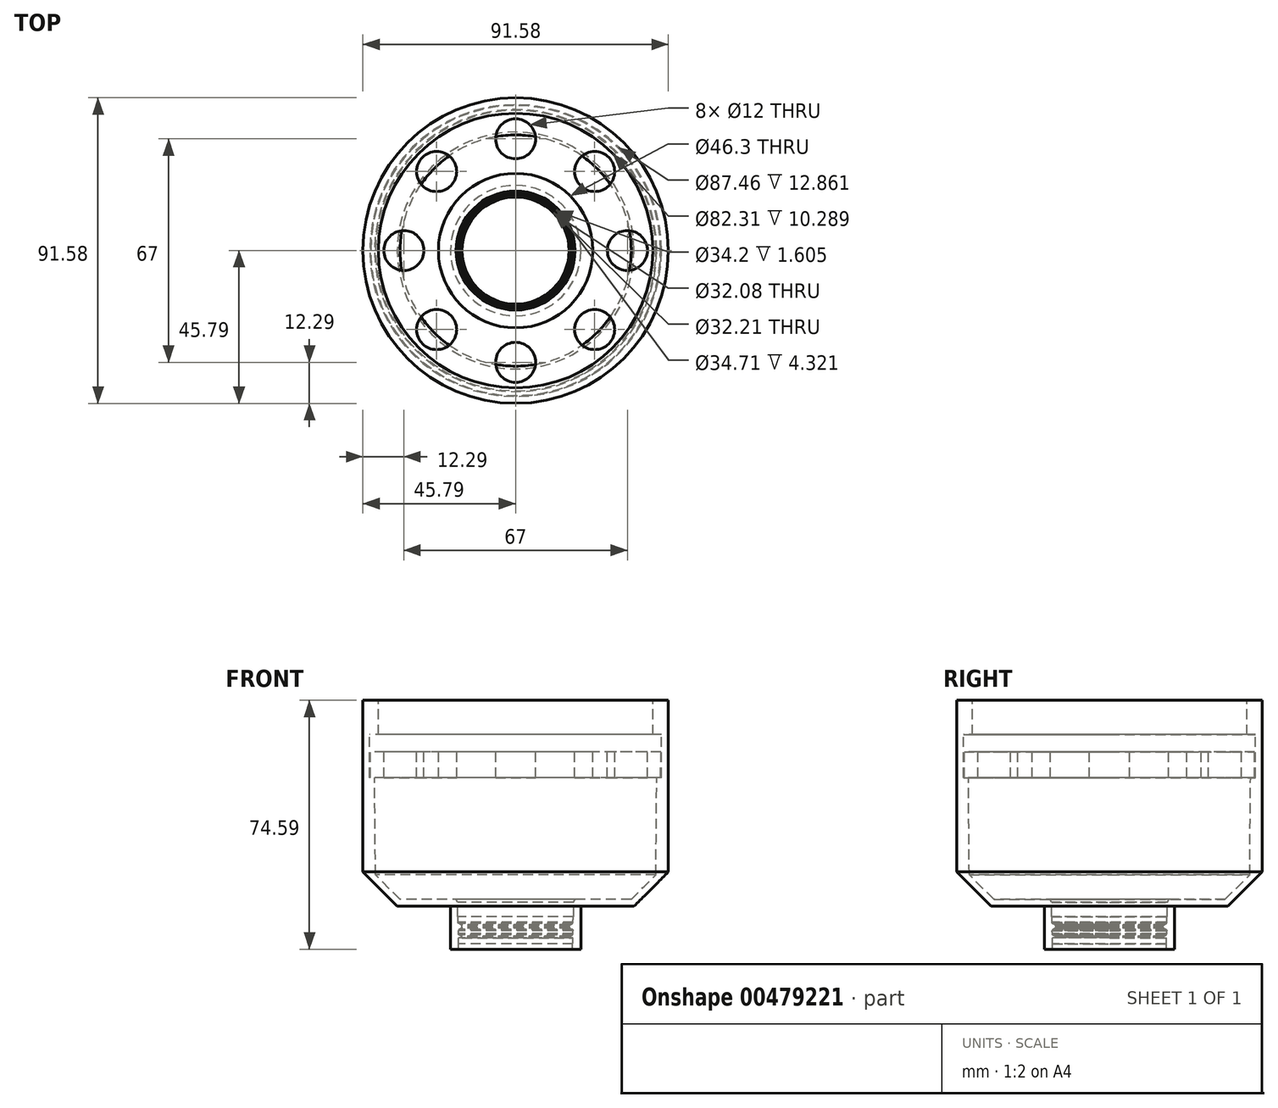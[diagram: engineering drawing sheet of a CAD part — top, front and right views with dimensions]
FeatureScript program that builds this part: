
annotation { "Feature Type Name" : "Feature", "Feature Type Description" : "" }
export const myFeature = defineFeature(function(context is Context, id is Id, definition is map)
    precondition{}
    {
        {
            var Q0;
            Q0=qCreatedBy(makeId("Front.planeOp"),FACE);
            var sketch = newSketch(context, id + "F0", { "sketchPlane" : qUnion([Q0])});
            skLineSegment(sketch, "E0", {"start": v(41.16, 37.94) * mm, "end": v(45.79, 37.94) * mm});
            skLineSegment(sketch, "E1", {"start": v(43.73, 25.08) * mm, "end": v(43.73, 27.65) * mm});
            skLineSegment(sketch, "E2", {"start": v(43.73, 27.65) * mm, "end": v(41.16, 27.65) * mm});
            skLineSegment(sketch, "E3", {"start": v(41.16, 27.65) * mm, "end": v(41.16, 37.94) * mm});
            skLineSegment(sketch, "E4", {"start": v(-41.16, 22.5) * mm, "end": v(-33.44, 22.5) * mm});
            skLineSegment(sketch, "E5", {"start": v(-43.73, 27.65) * mm, "end": v(-43.73, 25.08) * mm});
            skLineSegment(sketch, "E6", {"start": v(-41.16, 27.65) * mm, "end": v(-43.73, 27.65) * mm});
            skLineSegment(sketch, "E7", {"start": v(33.44, 22.5) * mm, "end": v(23.15, 22.5) * mm});
            skLineSegment(sketch, "E8", {"start": v(-41.16, 37.94) * mm, "end": v(-41.16, 27.65) * mm});
            skLineSegment(sketch, "E9", {"start": v(33.44, 22.5) * mm, "end": v(41.16, 22.5) * mm});
            skLineSegment(sketch, "E10", {"start": v(-23.15, 22.5) * mm, "end": v(-33.44, 22.5) * mm});
            skLineSegment(sketch, "E11", {"start": v(-43.73, 37.94) * mm, "end": v(-45.79, 37.94) * mm});
            skLineSegment(sketch, "E12", {"start": v(45.79, 37.94) * mm, "end": v(43.73, 37.94) * mm});
            skLineSegment(sketch, "E13", {"start": v(17.1, -36.65) * mm, "end": v(19.55, -36.65) * mm});
            skLineSegment(sketch, "E14", {"start": v(17.83, -21.74) * mm, "end": v(17.36, -22.56) * mm});
            skLineSegment(sketch, "E15", {"start": v(-38.42, 20.45) * mm, "end": v(-23.15, 20.45) * mm});
            skLineSegment(sketch, "E16", {"start": v(-41.42, 14.8) * mm, "end": v(-23.15, 14.8) * mm});
            skLineSegment(sketch, "E17", {"start": v(-17.83, -21.74) * mm, "end": v(-34.64, -21.74) * mm});
            skLineSegment(sketch, "E18", {"start": v(-35.5, -23.8) * mm, "end": v(-19.55, -23.8) * mm});
            skLineSegment(sketch, "E19", {"start": v(-23.15, 22.5) * mm, "end": v(-38.4, 22.5) * mm});
            skLineSegment(sketch, "E20", {"start": v(-38.4, 22.5) * mm, "end": v(-43.55, 22.5) * mm});
            skLineSegment(sketch, "E21", {"start": v(-38.42, 20.45) * mm, "end": v(-38.4, 22.5) * mm});
            skLineSegment(sketch, "E22", {"start": v(-41.37, 20.45) * mm, "end": v(-38.42, 20.45) * mm});
            skLineSegment(sketch, "E23", {"start": v(-41.42, 14.8) * mm, "end": v(-41.37, 20.45) * mm});
            skLineSegment(sketch, "E24", {"start": v(-43.48, 14.8) * mm, "end": v(-41.42, 14.8) * mm});
            skLineSegment(sketch, "E25", {"start": v(-43.55, 22.5) * mm, "end": v(-43.48, 14.8) * mm});
            skLineSegment(sketch, "E26", {"start": v(-45.79, 37.94) * mm, "end": v(-45.79, -13.5) * mm});
            skLineSegment(sketch, "E27", {"start": v(-43.73, 14.8) * mm, "end": v(-43.73, 37.94) * mm});
            skLineSegment(sketch, "E28", {"start": v(-42.29, 14.8) * mm, "end": v(-43.73, 14.8) * mm});
            skLineSegment(sketch, "E29", {"start": v(-42.03, -14.35) * mm, "end": v(-42.29, 14.8) * mm});
            skLineSegment(sketch, "E30", {"start": v(-34.64, -21.74) * mm, "end": v(-42.03, -14.35) * mm});
            skLineSegment(sketch, "E31", {"start": v(-45.79, -13.5) * mm, "end": v(-35.5, -23.8) * mm});
            skLineSegment(sketch, "E32", {"start": v(-19.57, -23.8) * mm, "end": v(-23.15, -23.8) * mm});
            skLineSegment(sketch, "E33", {"start": v(16.63, -30.81) * mm, "end": v(16.63, -30.81) * mm});
            skLineSegment(sketch, "E34", {"start": v(16.63, -30.81) * mm, "end": v(16.64, -30.81) * mm});
            skLineSegment(sketch, "E35", {"start": v(16.64, -30.81) * mm, "end": v(16.64, -30.82) * mm});
            skLineSegment(sketch, "E36", {"start": v(16.64, -30.82) * mm, "end": v(16.64, -30.82) * mm});
            skLineSegment(sketch, "E37", {"start": v(16.64, -30.82) * mm, "end": v(16.65, -30.82) * mm});
            skLineSegment(sketch, "E38", {"start": v(16.65, -30.82) * mm, "end": v(16.65, -30.82) * mm});
            skLineSegment(sketch, "E39", {"start": v(16.66, -30.84) * mm, "end": v(16.66, -30.84) * mm});
            skLineSegment(sketch, "E40", {"start": v(16.66, -30.84) * mm, "end": v(16.66, -30.83) * mm});
            skLineSegment(sketch, "E41", {"start": v(16.66, -30.83) * mm, "end": v(16.66, -30.83) * mm});
            skLineSegment(sketch, "E42", {"start": v(16.66, -30.83) * mm, "end": v(16.65, -30.83) * mm});
            skLineSegment(sketch, "E43", {"start": v(16.65, -30.83) * mm, "end": v(16.65, -30.83) * mm});
            skLineSegment(sketch, "E44", {"start": v(16.65, -30.83) * mm, "end": v(16.65, -30.82) * mm});
            skLineSegment(sketch, "E45", {"start": v(16.65, -30.82) * mm, "end": v(16.64, -30.82) * mm});
            skLineSegment(sketch, "E46", {"start": v(16.64, -30.82) * mm, "end": v(16.64, -30.81) * mm});
            skLineSegment(sketch, "E47", {"start": v(16.64, -30.81) * mm, "end": v(16.63, -30.81) * mm});
            skLineSegment(sketch, "E48", {"start": v(17.24, -26.88) * mm, "end": v(17.24, -26.88) * mm});
            skLineSegment(sketch, "E49", {"start": v(17.17, -29.4) * mm, "end": v(17.17, -29.38) * mm});
            skLineSegment(sketch, "E50", {"start": v(17.17, -29.38) * mm, "end": v(17.17, -29.37) * mm});
            skLineSegment(sketch, "E51", {"start": v(17.17, -29.37) * mm, "end": v(17.17, -29.36) * mm});
            skLineSegment(sketch, "E52", {"start": v(17.17, -29.36) * mm, "end": v(17.17, -29.35) * mm});
            skLineSegment(sketch, "E53", {"start": v(17.17, -29.35) * mm, "end": v(17.17, -29.34) * mm});
            skLineSegment(sketch, "E54", {"start": v(17.17, -29.34) * mm, "end": v(17.16, -29.32) * mm});
            skLineSegment(sketch, "E55", {"start": v(17.16, -29.32) * mm, "end": v(17.16, -29.31) * mm});
            skLineSegment(sketch, "E56", {"start": v(17.16, -29.31) * mm, "end": v(17.16, -29.3) * mm});
            skLineSegment(sketch, "E57", {"start": v(17.16, -29.3) * mm, "end": v(17.16, -29.29) * mm});
            skLineSegment(sketch, "E58", {"start": v(17.16, -29.29) * mm, "end": v(17.16, -29.28) * mm});
            skLineSegment(sketch, "E59", {"start": v(17.16, -29.28) * mm, "end": v(17.15, -29.27) * mm});
            skLineSegment(sketch, "E60", {"start": v(17.15, -29.27) * mm, "end": v(17.15, -29.26) * mm});
            skLineSegment(sketch, "E61", {"start": v(17.15, -29.26) * mm, "end": v(17.14, -29.24) * mm});
            skLineSegment(sketch, "E62", {"start": v(17.14, -29.24) * mm, "end": v(17.14, -29.23) * mm});
            skLineSegment(sketch, "E63", {"start": v(17.14, -29.23) * mm, "end": v(17.14, -29.22) * mm});
            skLineSegment(sketch, "E64", {"start": v(17.14, -29.22) * mm, "end": v(17.13, -29.21) * mm});
            skLineSegment(sketch, "E65", {"start": v(17.13, -29.21) * mm, "end": v(17.13, -29.2) * mm});
            skLineSegment(sketch, "E66", {"start": v(17.13, -29.2) * mm, "end": v(17.12, -29.2) * mm});
            skLineSegment(sketch, "E67", {"start": v(17.12, -29.2) * mm, "end": v(17.12, -29.18) * mm});
            skLineSegment(sketch, "E68", {"start": v(17.12, -29.18) * mm, "end": v(17.11, -29.18) * mm});
            skLineSegment(sketch, "E69", {"start": v(17.11, -29.18) * mm, "end": v(17.1, -29.17) * mm});
            skLineSegment(sketch, "E70", {"start": v(17.1, -29.17) * mm, "end": v(17.1, -29.16) * mm});
            skLineSegment(sketch, "E71", {"start": v(17.1, -29.16) * mm, "end": v(17.1, -29.15) * mm});
            skLineSegment(sketch, "E72", {"start": v(17.1, -29.15) * mm, "end": v(17.09, -29.14) * mm});
            skLineSegment(sketch, "E73", {"start": v(16.23, -27.73) * mm, "end": v(16.24, -27.73) * mm});
            skLineSegment(sketch, "E74", {"start": v(16.24, -27.73) * mm, "end": v(16.24, -27.72) * mm});
            skLineSegment(sketch, "E75", {"start": v(16.24, -27.72) * mm, "end": v(16.25, -27.72) * mm});
            skLineSegment(sketch, "E76", {"start": v(16.25, -27.72) * mm, "end": v(16.25, -27.71) * mm});
            skLineSegment(sketch, "E77", {"start": v(16.25, -27.71) * mm, "end": v(16.25, -27.71) * mm});
            skLineSegment(sketch, "E78", {"start": v(16.25, -27.71) * mm, "end": v(16.26, -27.7) * mm});
            skLineSegment(sketch, "E79", {"start": v(16.26, -27.7) * mm, "end": v(16.26, -27.7) * mm});
            skLineSegment(sketch, "E80", {"start": v(16.26, -27.7) * mm, "end": v(16.27, -27.7) * mm});
            skLineSegment(sketch, "E81", {"start": v(16.27, -27.7) * mm, "end": v(16.27, -27.7) * mm});
            skLineSegment(sketch, "E82", {"start": v(16.27, -27.7) * mm, "end": v(16.27, -27.69) * mm});
            skLineSegment(sketch, "E83", {"start": v(16.27, -27.69) * mm, "end": v(16.28, -27.69) * mm});
            skLineSegment(sketch, "E84", {"start": v(16.28, -27.69) * mm, "end": v(16.28, -27.68) * mm});
            skLineSegment(sketch, "E85", {"start": v(16.28, -27.68) * mm, "end": v(16.29, -27.68) * mm});
            skLineSegment(sketch, "E86", {"start": v(16.29, -27.68) * mm, "end": v(16.3, -27.67) * mm});
            skLineSegment(sketch, "E87", {"start": v(16.3, -27.67) * mm, "end": v(16.3, -27.67) * mm});
            skLineSegment(sketch, "E88", {"start": v(16.3, -27.67) * mm, "end": v(16.3, -27.66) * mm});
            skLineSegment(sketch, "E89", {"start": v(16.3, -27.66) * mm, "end": v(16.31, -27.66) * mm});
            skLineSegment(sketch, "E90", {"start": v(16.31, -27.66) * mm, "end": v(16.32, -27.66) * mm});
            skLineSegment(sketch, "E91", {"start": v(16.32, -27.66) * mm, "end": v(16.32, -27.65) * mm});
            skLineSegment(sketch, "E92", {"start": v(16.32, -27.65) * mm, "end": v(16.32, -27.65) * mm});
            skLineSegment(sketch, "E93", {"start": v(16.32, -27.65) * mm, "end": v(16.33, -27.65) * mm});
            skLineSegment(sketch, "E94", {"start": v(16.33, -27.65) * mm, "end": v(16.33, -27.65) * mm});
            skLineSegment(sketch, "E95", {"start": v(16.33, -27.65) * mm, "end": v(16.34, -27.64) * mm});
            skLineSegment(sketch, "E96", {"start": v(16.34, -27.64) * mm, "end": v(16.37, -27.62) * mm});
            skLineSegment(sketch, "E97", {"start": v(16.37, -27.62) * mm, "end": v(16.4, -27.6) * mm});
            skLineSegment(sketch, "E98", {"start": v(16.4, -27.6) * mm, "end": v(16.42, -27.59) * mm});
            skLineSegment(sketch, "E99", {"start": v(16.42, -27.59) * mm, "end": v(16.45, -27.57) * mm});
            skLineSegment(sketch, "E100", {"start": v(16.45, -27.57) * mm, "end": v(16.48, -27.55) * mm});
            skLineSegment(sketch, "E101", {"start": v(16.48, -27.55) * mm, "end": v(16.5, -27.54) * mm});
            skLineSegment(sketch, "E102", {"start": v(16.5, -27.54) * mm, "end": v(16.54, -27.52) * mm});
            skLineSegment(sketch, "E103", {"start": v(16.54, -27.52) * mm, "end": v(16.57, -27.5) * mm});
            skLineSegment(sketch, "E104", {"start": v(16.57, -27.5) * mm, "end": v(16.6, -27.48) * mm});
            skLineSegment(sketch, "E105", {"start": v(16.6, -27.48) * mm, "end": v(16.62, -27.47) * mm});
            skLineSegment(sketch, "E106", {"start": v(16.62, -27.47) * mm, "end": v(16.65, -27.45) * mm});
            skLineSegment(sketch, "E107", {"start": v(16.65, -27.45) * mm, "end": v(16.68, -27.43) * mm});
            skLineSegment(sketch, "E108", {"start": v(16.68, -27.43) * mm, "end": v(16.7, -27.41) * mm});
            skLineSegment(sketch, "E109", {"start": v(16.7, -27.41) * mm, "end": v(16.74, -27.4) * mm});
            skLineSegment(sketch, "E110", {"start": v(16.74, -27.4) * mm, "end": v(16.76, -27.38) * mm});
            skLineSegment(sketch, "E111", {"start": v(16.76, -27.38) * mm, "end": v(16.8, -27.36) * mm});
            skLineSegment(sketch, "E112", {"start": v(16.8, -27.36) * mm, "end": v(16.82, -27.34) * mm});
            skLineSegment(sketch, "E113", {"start": v(16.82, -27.34) * mm, "end": v(16.85, -27.32) * mm});
            skLineSegment(sketch, "E114", {"start": v(16.85, -27.32) * mm, "end": v(16.88, -27.3) * mm});
            skLineSegment(sketch, "E115", {"start": v(16.88, -27.3) * mm, "end": v(16.9, -27.29) * mm});
            skLineSegment(sketch, "E116", {"start": v(16.9, -27.29) * mm, "end": v(16.93, -27.27) * mm});
            skLineSegment(sketch, "E117", {"start": v(16.93, -27.27) * mm, "end": v(16.96, -27.25) * mm});
            skLineSegment(sketch, "E118", {"start": v(16.96, -27.25) * mm, "end": v(17, -27.23) * mm});
            skLineSegment(sketch, "E119", {"start": v(17, -27.23) * mm, "end": v(17.02, -27.22) * mm});
            skLineSegment(sketch, "E120", {"start": v(17.02, -27.22) * mm, "end": v(17.02, -27.21) * mm});
            skLineSegment(sketch, "E121", {"start": v(17.02, -27.21) * mm, "end": v(17.02, -27.21) * mm});
            skLineSegment(sketch, "E122", {"start": v(17.02, -27.21) * mm, "end": v(17.03, -27.21) * mm});
            skLineSegment(sketch, "E123", {"start": v(17.03, -27.21) * mm, "end": v(17.03, -27.2) * mm});
            skLineSegment(sketch, "E124", {"start": v(17.03, -27.2) * mm, "end": v(17.03, -27.2) * mm});
            skLineSegment(sketch, "E125", {"start": v(17.03, -27.2) * mm, "end": v(17.04, -27.2) * mm});
            skLineSegment(sketch, "E126", {"start": v(17.04, -27.2) * mm, "end": v(17.04, -27.2) * mm});
            skLineSegment(sketch, "E127", {"start": v(17.04, -27.2) * mm, "end": v(17.05, -27.2) * mm});
            skLineSegment(sketch, "E128", {"start": v(17.05, -27.2) * mm, "end": v(17.05, -27.2) * mm});
            skLineSegment(sketch, "E129", {"start": v(17.05, -27.2) * mm, "end": v(17.06, -27.19) * mm});
            skLineSegment(sketch, "E130", {"start": v(17.06, -27.19) * mm, "end": v(17.06, -27.19) * mm});
            skLineSegment(sketch, "E131", {"start": v(17.06, -27.19) * mm, "end": v(17.06, -27.18) * mm});
            skLineSegment(sketch, "E132", {"start": v(17.06, -27.18) * mm, "end": v(17.06, -27.18) * mm});
            skLineSegment(sketch, "E133", {"start": v(17.06, -27.18) * mm, "end": v(17.07, -27.18) * mm});
            skLineSegment(sketch, "E134", {"start": v(17.07, -27.18) * mm, "end": v(17.07, -27.18) * mm});
            skLineSegment(sketch, "E135", {"start": v(17.07, -27.18) * mm, "end": v(17.07, -27.17) * mm});
            skLineSegment(sketch, "E136", {"start": v(17.07, -27.17) * mm, "end": v(17.07, -27.17) * mm});
            skLineSegment(sketch, "E137", {"start": v(17.07, -27.17) * mm, "end": v(17.08, -27.17) * mm});
            skLineSegment(sketch, "E138", {"start": v(17.08, -27.17) * mm, "end": v(17.09, -27.16) * mm});
            skLineSegment(sketch, "E139", {"start": v(17.09, -27.16) * mm, "end": v(17.1, -27.15) * mm});
            skLineSegment(sketch, "E140", {"start": v(17.1, -27.15) * mm, "end": v(17.1, -27.14) * mm});
            skLineSegment(sketch, "E141", {"start": v(17.1, -27.14) * mm, "end": v(17.11, -27.13) * mm});
            skLineSegment(sketch, "E142", {"start": v(17.11, -27.13) * mm, "end": v(17.12, -27.12) * mm});
            skLineSegment(sketch, "E143", {"start": v(17.12, -27.12) * mm, "end": v(17.13, -27.11) * mm});
            skLineSegment(sketch, "E144", {"start": v(17.13, -27.11) * mm, "end": v(17.13, -27.1) * mm});
            skLineSegment(sketch, "E145", {"start": v(17.13, -27.1) * mm, "end": v(17.14, -27.1) * mm});
            skLineSegment(sketch, "E146", {"start": v(17.14, -27.1) * mm, "end": v(17.15, -27.08) * mm});
            skLineSegment(sketch, "E147", {"start": v(17.15, -27.08) * mm, "end": v(17.16, -27.07) * mm});
            skLineSegment(sketch, "E148", {"start": v(17.16, -27.07) * mm, "end": v(17.16, -27.06) * mm});
            skLineSegment(sketch, "E149", {"start": v(17.16, -27.06) * mm, "end": v(17.17, -27.05) * mm});
            skLineSegment(sketch, "E150", {"start": v(17.17, -27.05) * mm, "end": v(17.17, -27.03) * mm});
            skLineSegment(sketch, "E151", {"start": v(17.17, -27.03) * mm, "end": v(17.18, -27.02) * mm});
            skLineSegment(sketch, "E152", {"start": v(17.18, -27.02) * mm, "end": v(17.19, -27) * mm});
            skLineSegment(sketch, "E153", {"start": v(17.19, -27) * mm, "end": v(17.2, -27) * mm});
            skLineSegment(sketch, "E154", {"start": v(17.2, -27) * mm, "end": v(17.2, -26.98) * mm});
            skLineSegment(sketch, "E155", {"start": v(17.2, -26.98) * mm, "end": v(17.2, -26.97) * mm});
            skLineSegment(sketch, "E156", {"start": v(17.2, -26.97) * mm, "end": v(17.2, -26.95) * mm});
            skLineSegment(sketch, "E157", {"start": v(17.2, -26.95) * mm, "end": v(17.2, -26.94) * mm});
            skLineSegment(sketch, "E158", {"start": v(17.2, -26.94) * mm, "end": v(17.2, -26.92) * mm});
            skLineSegment(sketch, "E159", {"start": v(17.2, -26.92) * mm, "end": v(17.21, -26.9) * mm});
            skLineSegment(sketch, "E160", {"start": v(17.21, -26.9) * mm, "end": v(17.21, -26.9) * mm});
            skLineSegment(sketch, "E161", {"start": v(17.21, -26.9) * mm, "end": v(17.21, -26.88) * mm});
            skLineSegment(sketch, "E162", {"start": v(17.2, -29.43) * mm, "end": v(17.2, -29.43) * mm});
            skLineSegment(sketch, "E163", {"start": v(17.2, -29.43) * mm, "end": v(17.2, -29.42) * mm});
            skLineSegment(sketch, "E164", {"start": v(17.2, -29.42) * mm, "end": v(17.2, -29.42) * mm});
            skLineSegment(sketch, "E165", {"start": v(17.2, -29.42) * mm, "end": v(17.2, -29.41) * mm});
            skLineSegment(sketch, "E166", {"start": v(17.2, -29.41) * mm, "end": v(17.2, -29.41) * mm});
            skLineSegment(sketch, "E167", {"start": v(17.2, -29.41) * mm, "end": v(17.19, -29.4) * mm});
            skLineSegment(sketch, "E168", {"start": v(17.19, -29.4) * mm, "end": v(17.19, -29.4) * mm});
            skLineSegment(sketch, "E169", {"start": v(17.19, -29.4) * mm, "end": v(17.18, -29.4) * mm});
            skLineSegment(sketch, "E170", {"start": v(17.18, -29.4) * mm, "end": v(17.18, -29.4) * mm});
            skLineSegment(sketch, "E171", {"start": v(17.18, -29.4) * mm, "end": v(17.17, -29.4) * mm});
            skLineSegment(sketch, "E172", {"start": v(17.17, -29.4) * mm, "end": v(17.17, -29.4) * mm});
            skLineSegment(sketch, "E173", {"start": v(17.02, -27.22) * mm, "end": v(17.02, -27.22) * mm});
            skLineSegment(sketch, "E174", {"start": v(17.02, -27.22) * mm, "end": v(17.03, -27.22) * mm});
            skLineSegment(sketch, "E175", {"start": v(17.03, -27.22) * mm, "end": v(17.03, -27.22) * mm});
            skLineSegment(sketch, "E176", {"start": v(17.03, -27.22) * mm, "end": v(17.03, -27.23) * mm});
            skLineSegment(sketch, "E177", {"start": v(17.03, -27.23) * mm, "end": v(17.03, -27.23) * mm});
            skLineSegment(sketch, "E178", {"start": v(17.03, -27.23) * mm, "end": v(17.04, -27.23) * mm});
            skLineSegment(sketch, "E179", {"start": v(17.04, -27.23) * mm, "end": v(17.04, -27.23) * mm});
            skLineSegment(sketch, "E180", {"start": v(17.04, -27.23) * mm, "end": v(17.04, -27.24) * mm});
            skLineSegment(sketch, "E181", {"start": v(17.04, -27.24) * mm, "end": v(17.04, -27.24) * mm});
            skLineSegment(sketch, "E182", {"start": v(17.24, -26.88) * mm, "end": v(17.23, -26.88) * mm});
            skLineSegment(sketch, "E183", {"start": v(17.23, -26.88) * mm, "end": v(17.23, -26.88) * mm});
            skLineSegment(sketch, "E184", {"start": v(17.23, -26.88) * mm, "end": v(17.22, -26.88) * mm});
            skLineSegment(sketch, "E185", {"start": v(17.22, -26.88) * mm, "end": v(17.22, -26.88) * mm});
            skLineSegment(sketch, "E186", {"start": v(17.22, -26.88) * mm, "end": v(17.21, -26.88) * mm});
            skLineSegment(sketch, "E187", {"start": v(17.21, -26.88) * mm, "end": v(17.21, -26.88) * mm});
            skLineSegment(sketch, "E188", {"start": v(17.24, -26.88) * mm, "end": v(17.24, -26.89) * mm});
            skLineSegment(sketch, "E189", {"start": v(17.24, -26.89) * mm, "end": v(17.24, -26.89) * mm});
            skLineSegment(sketch, "E190", {"start": v(17.24, -26.89) * mm, "end": v(17.24, -26.9) * mm});
            skLineSegment(sketch, "E191", {"start": v(17.24, -26.9) * mm, "end": v(17.24, -26.9) * mm});
            skLineSegment(sketch, "E192", {"start": v(-17.36, -22.56) * mm, "end": v(-17.83, -21.74) * mm});
            skLineSegment(sketch, "E193", {"start": v(-17.36, -26.88) * mm, "end": v(-17.36, -22.56) * mm});
            skLineSegment(sketch, "E194", {"start": v(-17.24, -26.88) * mm, "end": v(-17.36, -26.88) * mm});
            skLineSegment(sketch, "E195", {"start": v(-17.21, -28.6) * mm, "end": v(-17.24, -26.88) * mm});
            skLineSegment(sketch, "E196", {"start": v(-17, -28.96) * mm, "end": v(-17.02, -28.95) * mm});
            skLineSegment(sketch, "E197", {"start": v(-17.02, -28.95) * mm, "end": v(-17.04, -28.94) * mm});
            skLineSegment(sketch, "E198", {"start": v(-17.04, -28.94) * mm, "end": v(-17.05, -28.93) * mm});
            skLineSegment(sketch, "E199", {"start": v(-17.05, -28.93) * mm, "end": v(-17.07, -28.92) * mm});
            skLineSegment(sketch, "E200", {"start": v(-17.07, -28.92) * mm, "end": v(-17.08, -28.9) * mm});
            skLineSegment(sketch, "E201", {"start": v(-17.08, -28.9) * mm, "end": v(-17.1, -28.9) * mm});
            skLineSegment(sketch, "E202", {"start": v(-17.1, -28.9) * mm, "end": v(-17.1, -28.88) * mm});
            skLineSegment(sketch, "E203", {"start": v(-17.1, -28.88) * mm, "end": v(-17.12, -28.87) * mm});
            skLineSegment(sketch, "E204", {"start": v(-17.12, -28.87) * mm, "end": v(-17.13, -28.85) * mm});
            skLineSegment(sketch, "E205", {"start": v(-17.13, -28.85) * mm, "end": v(-17.14, -28.84) * mm});
            skLineSegment(sketch, "E206", {"start": v(-17.14, -28.84) * mm, "end": v(-17.15, -28.82) * mm});
            skLineSegment(sketch, "E207", {"start": v(-17.15, -28.82) * mm, "end": v(-17.16, -28.8) * mm});
            skLineSegment(sketch, "E208", {"start": v(-17.16, -28.8) * mm, "end": v(-17.17, -28.8) * mm});
            skLineSegment(sketch, "E209", {"start": v(-17.17, -28.8) * mm, "end": v(-17.17, -28.78) * mm});
            skLineSegment(sketch, "E210", {"start": v(-17.17, -28.78) * mm, "end": v(-17.18, -28.76) * mm});
            skLineSegment(sketch, "E211", {"start": v(-17.18, -28.76) * mm, "end": v(-17.19, -28.75) * mm});
            skLineSegment(sketch, "E212", {"start": v(-17.19, -28.75) * mm, "end": v(-17.2, -28.73) * mm});
            skLineSegment(sketch, "E213", {"start": v(-17.2, -28.73) * mm, "end": v(-17.2, -28.71) * mm});
            skLineSegment(sketch, "E214", {"start": v(-17.2, -28.71) * mm, "end": v(-17.2, -28.7) * mm});
            skLineSegment(sketch, "E215", {"start": v(-17.2, -28.7) * mm, "end": v(-17.2, -28.68) * mm});
            skLineSegment(sketch, "E216", {"start": v(-17.2, -28.68) * mm, "end": v(-17.2, -28.66) * mm});
            skLineSegment(sketch, "E217", {"start": v(-17.2, -28.66) * mm, "end": v(-17.21, -28.64) * mm});
            skLineSegment(sketch, "E218", {"start": v(-17.21, -28.64) * mm, "end": v(-17.21, -28.62) * mm});
            skLineSegment(sketch, "E219", {"start": v(-17.21, -28.62) * mm, "end": v(-17.21, -28.6) * mm});
            skLineSegment(sketch, "E220", {"start": v(-16.3, -29.36) * mm, "end": v(-16.34, -29.34) * mm});
            skLineSegment(sketch, "E221", {"start": v(-16.34, -29.34) * mm, "end": v(-16.37, -29.33) * mm});
            skLineSegment(sketch, "E222", {"start": v(-16.37, -29.33) * mm, "end": v(-16.4, -29.31) * mm});
            skLineSegment(sketch, "E223", {"start": v(-16.4, -29.31) * mm, "end": v(-16.43, -29.3) * mm});
            skLineSegment(sketch, "E224", {"start": v(-16.43, -29.3) * mm, "end": v(-16.45, -29.28) * mm});
            skLineSegment(sketch, "E225", {"start": v(-16.45, -29.28) * mm, "end": v(-16.48, -29.26) * mm});
            skLineSegment(sketch, "E226", {"start": v(-16.48, -29.26) * mm, "end": v(-16.51, -29.24) * mm});
            skLineSegment(sketch, "E227", {"start": v(-16.51, -29.24) * mm, "end": v(-16.54, -29.23) * mm});
            skLineSegment(sketch, "E228", {"start": v(-16.54, -29.23) * mm, "end": v(-16.57, -29.2) * mm});
            skLineSegment(sketch, "E229", {"start": v(-16.57, -29.2) * mm, "end": v(-16.6, -29.2) * mm});
            skLineSegment(sketch, "E230", {"start": v(-16.6, -29.2) * mm, "end": v(-16.63, -29.18) * mm});
            skLineSegment(sketch, "E231", {"start": v(-16.63, -29.18) * mm, "end": v(-16.66, -29.16) * mm});
            skLineSegment(sketch, "E232", {"start": v(-16.66, -29.16) * mm, "end": v(-16.69, -29.14) * mm});
            skLineSegment(sketch, "E233", {"start": v(-16.69, -29.14) * mm, "end": v(-16.72, -29.12) * mm});
            skLineSegment(sketch, "E234", {"start": v(-16.72, -29.12) * mm, "end": v(-16.75, -29.1) * mm});
            skLineSegment(sketch, "E235", {"start": v(-16.75, -29.1) * mm, "end": v(-16.77, -29.1) * mm});
            skLineSegment(sketch, "E236", {"start": v(-16.77, -29.1) * mm, "end": v(-16.8, -29.07) * mm});
            skLineSegment(sketch, "E237", {"start": v(-16.8, -29.07) * mm, "end": v(-16.83, -29.06) * mm});
            skLineSegment(sketch, "E238", {"start": v(-16.83, -29.06) * mm, "end": v(-16.86, -29.04) * mm});
            skLineSegment(sketch, "E239", {"start": v(-16.86, -29.04) * mm, "end": v(-16.9, -29.02) * mm});
            skLineSegment(sketch, "E240", {"start": v(-16.9, -29.02) * mm, "end": v(-16.92, -29) * mm});
            skLineSegment(sketch, "E241", {"start": v(-16.92, -29) * mm, "end": v(-16.95, -29) * mm});
            skLineSegment(sketch, "E242", {"start": v(-16.95, -29) * mm, "end": v(-16.98, -28.97) * mm});
            skLineSegment(sketch, "E243", {"start": v(-16.98, -28.97) * mm, "end": v(-17, -28.96) * mm});
            skLineSegment(sketch, "E244", {"start": v(-16.1, -29.72) * mm, "end": v(-16.1, -29.7) * mm});
            skLineSegment(sketch, "E245", {"start": v(-16.1, -29.7) * mm, "end": v(-16.1, -29.68) * mm});
            skLineSegment(sketch, "E246", {"start": v(-16.1, -29.68) * mm, "end": v(-16.1, -29.66) * mm});
            skLineSegment(sketch, "E247", {"start": v(-16.1, -29.66) * mm, "end": v(-16.1, -29.65) * mm});
            skLineSegment(sketch, "E248", {"start": v(-16.1, -29.65) * mm, "end": v(-16.11, -29.63) * mm});
            skLineSegment(sketch, "E249", {"start": v(-16.11, -29.63) * mm, "end": v(-16.12, -29.61) * mm});
            skLineSegment(sketch, "E250", {"start": v(-16.12, -29.61) * mm, "end": v(-16.12, -29.6) * mm});
            skLineSegment(sketch, "E251", {"start": v(-16.12, -29.6) * mm, "end": v(-16.13, -29.58) * mm});
            skLineSegment(sketch, "E252", {"start": v(-16.13, -29.58) * mm, "end": v(-16.13, -29.56) * mm});
            skLineSegment(sketch, "E253", {"start": v(-16.13, -29.56) * mm, "end": v(-16.14, -29.54) * mm});
            skLineSegment(sketch, "E254", {"start": v(-16.14, -29.54) * mm, "end": v(-16.15, -29.53) * mm});
            skLineSegment(sketch, "E255", {"start": v(-16.15, -29.53) * mm, "end": v(-16.16, -29.51) * mm});
            skLineSegment(sketch, "E256", {"start": v(-16.16, -29.51) * mm, "end": v(-16.17, -29.5) * mm});
            skLineSegment(sketch, "E257", {"start": v(-16.17, -29.5) * mm, "end": v(-16.18, -29.48) * mm});
            skLineSegment(sketch, "E258", {"start": v(-16.18, -29.48) * mm, "end": v(-16.19, -29.47) * mm});
            skLineSegment(sketch, "E259", {"start": v(-16.19, -29.47) * mm, "end": v(-16.2, -29.45) * mm});
            skLineSegment(sketch, "E260", {"start": v(-16.2, -29.45) * mm, "end": v(-16.21, -29.44) * mm});
            skLineSegment(sketch, "E261", {"start": v(-16.21, -29.44) * mm, "end": v(-16.22, -29.43) * mm});
            skLineSegment(sketch, "E262", {"start": v(-16.22, -29.43) * mm, "end": v(-16.24, -29.41) * mm});
            skLineSegment(sketch, "E263", {"start": v(-16.24, -29.41) * mm, "end": v(-16.25, -29.4) * mm});
            skLineSegment(sketch, "E264", {"start": v(-16.25, -29.4) * mm, "end": v(-16.26, -29.4) * mm});
            skLineSegment(sketch, "E265", {"start": v(-16.26, -29.4) * mm, "end": v(-16.28, -29.38) * mm});
            skLineSegment(sketch, "E266", {"start": v(-16.28, -29.38) * mm, "end": v(-16.3, -29.37) * mm});
            skLineSegment(sketch, "E267", {"start": v(-16.3, -29.37) * mm, "end": v(-16.3, -29.36) * mm});
            skLineSegment(sketch, "E268", {"start": v(-16.1, -29.88) * mm, "end": v(-16.1, -29.87) * mm});
            skLineSegment(sketch, "E269", {"start": v(-16.1, -29.87) * mm, "end": v(-16.1, -29.87) * mm});
            skLineSegment(sketch, "E270", {"start": v(-16.1, -29.87) * mm, "end": v(-16.1, -29.86) * mm});
            skLineSegment(sketch, "E271", {"start": v(-16.1, -29.86) * mm, "end": v(-16.1, -29.85) * mm});
            skLineSegment(sketch, "E272", {"start": v(-16.1, -29.85) * mm, "end": v(-16.1, -29.85) * mm});
            skLineSegment(sketch, "E273", {"start": v(-16.1, -29.85) * mm, "end": v(-16.1, -29.84) * mm});
            skLineSegment(sketch, "E274", {"start": v(-16.1, -29.84) * mm, "end": v(-16.1, -29.83) * mm});
            skLineSegment(sketch, "E275", {"start": v(-16.1, -29.83) * mm, "end": v(-16.1, -29.83) * mm});
            skLineSegment(sketch, "E276", {"start": v(-16.1, -29.83) * mm, "end": v(-16.1, -29.82) * mm});
            skLineSegment(sketch, "E277", {"start": v(-16.1, -29.82) * mm, "end": v(-16.1, -29.81) * mm});
            skLineSegment(sketch, "E278", {"start": v(-16.1, -29.81) * mm, "end": v(-16.1, -29.8) * mm});
            skLineSegment(sketch, "E279", {"start": v(-16.1, -29.8) * mm, "end": v(-16.1, -29.8) * mm});
            skLineSegment(sketch, "E280", {"start": v(-16.1, -29.8) * mm, "end": v(-16.1, -29.79) * mm});
            skLineSegment(sketch, "E281", {"start": v(-16.1, -29.79) * mm, "end": v(-16.1, -29.78) * mm});
            skLineSegment(sketch, "E282", {"start": v(-16.1, -29.78) * mm, "end": v(-16.1, -29.77) * mm});
            skLineSegment(sketch, "E283", {"start": v(-16.1, -29.77) * mm, "end": v(-16.1, -29.76) * mm});
            skLineSegment(sketch, "E284", {"start": v(-16.1, -29.76) * mm, "end": v(-16.1, -29.76) * mm});
            skLineSegment(sketch, "E285", {"start": v(-16.1, -29.76) * mm, "end": v(-16.1, -29.75) * mm});
            skLineSegment(sketch, "E286", {"start": v(-16.1, -29.75) * mm, "end": v(-16.1, -29.74) * mm});
            skLineSegment(sketch, "E287", {"start": v(-16.1, -29.74) * mm, "end": v(-16.1, -29.74) * mm});
            skLineSegment(sketch, "E288", {"start": v(-16.1, -29.74) * mm, "end": v(-16.1, -29.73) * mm});
            skLineSegment(sketch, "E289", {"start": v(-16.1, -29.73) * mm, "end": v(-16.1, -29.72) * mm});
            skLineSegment(sketch, "E290", {"start": v(-16.1, -29.72) * mm, "end": v(-16.1, -29.72) * mm});
            skLineSegment(sketch, "E291", {"start": v(-16.1, -30.04) * mm, "end": v(-16.1, -30.04) * mm});
            skLineSegment(sketch, "E292", {"start": v(-16.1, -30.04) * mm, "end": v(-16.1, -30.03) * mm});
            skLineSegment(sketch, "E293", {"start": v(-16.1, -30.03) * mm, "end": v(-16.1, -30.02) * mm});
            skLineSegment(sketch, "E294", {"start": v(-16.1, -30.02) * mm, "end": v(-16.1, -30.02) * mm});
            skLineSegment(sketch, "E295", {"start": v(-16.1, -30.02) * mm, "end": v(-16.1, -30.01) * mm});
            skLineSegment(sketch, "E296", {"start": v(-16.1, -30.01) * mm, "end": v(-16.1, -30) * mm});
            skLineSegment(sketch, "E297", {"start": v(-16.1, -30) * mm, "end": v(-16.1, -30) * mm});
            skLineSegment(sketch, "E298", {"start": v(-16.1, -30) * mm, "end": v(-16.1, -29.99) * mm});
            skLineSegment(sketch, "E299", {"start": v(-16.1, -29.99) * mm, "end": v(-16.1, -29.98) * mm});
            skLineSegment(sketch, "E300", {"start": v(-16.1, -29.98) * mm, "end": v(-16.1, -29.98) * mm});
            skLineSegment(sketch, "E301", {"start": v(-16.1, -29.98) * mm, "end": v(-16.1, -29.97) * mm});
            skLineSegment(sketch, "E302", {"start": v(-16.1, -29.97) * mm, "end": v(-16.1, -29.96) * mm});
            skLineSegment(sketch, "E303", {"start": v(-16.1, -29.96) * mm, "end": v(-16.1, -29.96) * mm});
            skLineSegment(sketch, "E304", {"start": v(-16.1, -29.96) * mm, "end": v(-16.1, -29.95) * mm});
            skLineSegment(sketch, "E305", {"start": v(-16.1, -29.95) * mm, "end": v(-16.1, -29.94) * mm});
            skLineSegment(sketch, "E306", {"start": v(-16.1, -29.94) * mm, "end": v(-16.1, -29.94) * mm});
            skLineSegment(sketch, "E307", {"start": v(-16.1, -29.94) * mm, "end": v(-16.1, -29.93) * mm});
            skLineSegment(sketch, "E308", {"start": v(-16.1, -29.93) * mm, "end": v(-16.1, -29.92) * mm});
            skLineSegment(sketch, "E309", {"start": v(-16.1, -29.92) * mm, "end": v(-16.1, -29.91) * mm});
            skLineSegment(sketch, "E310", {"start": v(-16.1, -29.91) * mm, "end": v(-16.1, -29.9) * mm});
            skLineSegment(sketch, "E311", {"start": v(-16.1, -29.9) * mm, "end": v(-16.1, -29.9) * mm});
            skLineSegment(sketch, "E312", {"start": v(-16.1, -29.9) * mm, "end": v(-16.1, -29.89) * mm});
            skLineSegment(sketch, "E313", {"start": v(-16.1, -29.89) * mm, "end": v(-16.1, -29.88) * mm});
            skLineSegment(sketch, "E314", {"start": v(-16.3, -30.4) * mm, "end": v(-16.3, -30.4) * mm});
            skLineSegment(sketch, "E315", {"start": v(-16.3, -30.4) * mm, "end": v(-16.28, -30.38) * mm});
            skLineSegment(sketch, "E316", {"start": v(-16.28, -30.38) * mm, "end": v(-16.26, -30.37) * mm});
            skLineSegment(sketch, "E317", {"start": v(-16.26, -30.37) * mm, "end": v(-16.25, -30.36) * mm});
            skLineSegment(sketch, "E318", {"start": v(-16.25, -30.36) * mm, "end": v(-16.24, -30.35) * mm});
            skLineSegment(sketch, "E319", {"start": v(-16.24, -30.35) * mm, "end": v(-16.22, -30.34) * mm});
            skLineSegment(sketch, "E320", {"start": v(-16.22, -30.34) * mm, "end": v(-16.21, -30.32) * mm});
            skLineSegment(sketch, "E321", {"start": v(-16.21, -30.32) * mm, "end": v(-16.2, -30.3) * mm});
            skLineSegment(sketch, "E322", {"start": v(-16.2, -30.3) * mm, "end": v(-16.19, -30.3) * mm});
            skLineSegment(sketch, "E323", {"start": v(-16.19, -30.3) * mm, "end": v(-16.18, -30.28) * mm});
            skLineSegment(sketch, "E324", {"start": v(-16.18, -30.28) * mm, "end": v(-16.17, -30.27) * mm});
            skLineSegment(sketch, "E325", {"start": v(-16.17, -30.27) * mm, "end": v(-16.16, -30.25) * mm});
            skLineSegment(sketch, "E326", {"start": v(-16.16, -30.25) * mm, "end": v(-16.15, -30.23) * mm});
            skLineSegment(sketch, "E327", {"start": v(-16.15, -30.23) * mm, "end": v(-16.14, -30.22) * mm});
            skLineSegment(sketch, "E328", {"start": v(-16.14, -30.22) * mm, "end": v(-16.13, -30.2) * mm});
            skLineSegment(sketch, "E329", {"start": v(-16.13, -30.2) * mm, "end": v(-16.13, -30.18) * mm});
            skLineSegment(sketch, "E330", {"start": v(-16.13, -30.18) * mm, "end": v(-16.12, -30.17) * mm});
            skLineSegment(sketch, "E331", {"start": v(-16.12, -30.17) * mm, "end": v(-16.12, -30.15) * mm});
            skLineSegment(sketch, "E332", {"start": v(-16.12, -30.15) * mm, "end": v(-16.11, -30.13) * mm});
            skLineSegment(sketch, "E333", {"start": v(-16.11, -30.13) * mm, "end": v(-16.1, -30.12) * mm});
            skLineSegment(sketch, "E334", {"start": v(-16.1, -30.12) * mm, "end": v(-16.1, -30.1) * mm});
            skLineSegment(sketch, "E335", {"start": v(-16.1, -30.1) * mm, "end": v(-16.1, -30.08) * mm});
            skLineSegment(sketch, "E336", {"start": v(-16.1, -30.08) * mm, "end": v(-16.1, -30.06) * mm});
            skLineSegment(sketch, "E337", {"start": v(-16.1, -30.06) * mm, "end": v(-16.1, -30.04) * mm});
            skLineSegment(sketch, "E338", {"start": v(-16.96, -30.78) * mm, "end": v(-16.94, -30.76) * mm});
            skLineSegment(sketch, "E339", {"start": v(-16.94, -30.76) * mm, "end": v(-16.9, -30.75) * mm});
            skLineSegment(sketch, "E340", {"start": v(-16.9, -30.75) * mm, "end": v(-16.88, -30.73) * mm});
            skLineSegment(sketch, "E341", {"start": v(-16.88, -30.73) * mm, "end": v(-16.85, -30.72) * mm});
            skLineSegment(sketch, "E342", {"start": v(-16.85, -30.72) * mm, "end": v(-16.83, -30.7) * mm});
            skLineSegment(sketch, "E343", {"start": v(-16.83, -30.7) * mm, "end": v(-16.8, -30.68) * mm});
            skLineSegment(sketch, "E344", {"start": v(-16.8, -30.68) * mm, "end": v(-16.77, -30.67) * mm});
            skLineSegment(sketch, "E345", {"start": v(-16.77, -30.67) * mm, "end": v(-16.74, -30.65) * mm});
            skLineSegment(sketch, "E346", {"start": v(-16.74, -30.65) * mm, "end": v(-16.72, -30.64) * mm});
            skLineSegment(sketch, "E347", {"start": v(-16.72, -30.64) * mm, "end": v(-16.7, -30.62) * mm});
            skLineSegment(sketch, "E348", {"start": v(-16.7, -30.62) * mm, "end": v(-16.66, -30.6) * mm});
            skLineSegment(sketch, "E349", {"start": v(-16.66, -30.6) * mm, "end": v(-16.64, -30.59) * mm});
            skLineSegment(sketch, "E350", {"start": v(-16.64, -30.59) * mm, "end": v(-16.6, -30.57) * mm});
            skLineSegment(sketch, "E351", {"start": v(-16.6, -30.57) * mm, "end": v(-16.58, -30.56) * mm});
            skLineSegment(sketch, "E352", {"start": v(-16.58, -30.56) * mm, "end": v(-16.55, -30.54) * mm});
            skLineSegment(sketch, "E353", {"start": v(-16.55, -30.54) * mm, "end": v(-16.53, -30.53) * mm});
            skLineSegment(sketch, "E354", {"start": v(-16.53, -30.53) * mm, "end": v(-16.5, -30.51) * mm});
            skLineSegment(sketch, "E355", {"start": v(-16.5, -30.51) * mm, "end": v(-16.47, -30.5) * mm});
            skLineSegment(sketch, "E356", {"start": v(-16.47, -30.5) * mm, "end": v(-16.44, -30.48) * mm});
            skLineSegment(sketch, "E357", {"start": v(-16.44, -30.48) * mm, "end": v(-16.42, -30.46) * mm});
            skLineSegment(sketch, "E358", {"start": v(-16.42, -30.46) * mm, "end": v(-16.4, -30.45) * mm});
            skLineSegment(sketch, "E359", {"start": v(-16.4, -30.45) * mm, "end": v(-16.36, -30.43) * mm});
            skLineSegment(sketch, "E360", {"start": v(-16.36, -30.43) * mm, "end": v(-16.34, -30.42) * mm});
            skLineSegment(sketch, "E361", {"start": v(-16.34, -30.42) * mm, "end": v(-16.3, -30.4) * mm});
            skLineSegment(sketch, "E362", {"start": v(-17.17, -31.14) * mm, "end": v(-17.17, -31.12) * mm});
            skLineSegment(sketch, "E363", {"start": v(-17.17, -31.12) * mm, "end": v(-17.17, -31.1) * mm});
            skLineSegment(sketch, "E364", {"start": v(-17.17, -31.1) * mm, "end": v(-17.17, -31.09) * mm});
            skLineSegment(sketch, "E365", {"start": v(-17.17, -31.09) * mm, "end": v(-17.16, -31.07) * mm});
            skLineSegment(sketch, "E366", {"start": v(-17.16, -31.07) * mm, "end": v(-17.16, -31.05) * mm});
            skLineSegment(sketch, "E367", {"start": v(-17.16, -31.05) * mm, "end": v(-17.16, -31.03) * mm});
            skLineSegment(sketch, "E368", {"start": v(-17.16, -31.03) * mm, "end": v(-17.15, -31.02) * mm});
            skLineSegment(sketch, "E369", {"start": v(-17.15, -31.02) * mm, "end": v(-17.15, -31) * mm});
            skLineSegment(sketch, "E370", {"start": v(-17.15, -31) * mm, "end": v(-17.14, -30.98) * mm});
            skLineSegment(sketch, "E371", {"start": v(-17.14, -30.98) * mm, "end": v(-17.13, -30.97) * mm});
            skLineSegment(sketch, "E372", {"start": v(-17.13, -30.97) * mm, "end": v(-17.12, -30.95) * mm});
            skLineSegment(sketch, "E373", {"start": v(-17.12, -30.95) * mm, "end": v(-17.12, -30.93) * mm});
            skLineSegment(sketch, "E374", {"start": v(-17.12, -30.93) * mm, "end": v(-17.1, -30.92) * mm});
            skLineSegment(sketch, "E375", {"start": v(-17.1, -30.92) * mm, "end": v(-17.1, -30.9) * mm});
            skLineSegment(sketch, "E376", {"start": v(-17.1, -30.9) * mm, "end": v(-17.09, -30.89) * mm});
            skLineSegment(sketch, "E377", {"start": v(-17.09, -30.89) * mm, "end": v(-17.07, -30.87) * mm});
            skLineSegment(sketch, "E378", {"start": v(-17.07, -30.87) * mm, "end": v(-17.06, -30.86) * mm});
            skLineSegment(sketch, "E379", {"start": v(-17.06, -30.86) * mm, "end": v(-17.05, -30.85) * mm});
            skLineSegment(sketch, "E380", {"start": v(-17.05, -30.85) * mm, "end": v(-17.04, -30.83) * mm});
            skLineSegment(sketch, "E381", {"start": v(-17.04, -30.83) * mm, "end": v(-17.02, -30.82) * mm});
            skLineSegment(sketch, "E382", {"start": v(-17.02, -30.82) * mm, "end": v(-17, -30.8) * mm});
            skLineSegment(sketch, "E383", {"start": v(-17, -30.8) * mm, "end": v(-17, -30.8) * mm});
            skLineSegment(sketch, "E384", {"start": v(-17, -30.8) * mm, "end": v(-16.98, -30.79) * mm});
            skLineSegment(sketch, "E385", {"start": v(-16.98, -30.79) * mm, "end": v(-16.96, -30.78) * mm});
            skLineSegment(sketch, "E386", {"start": v(-17.15, -32.04) * mm, "end": v(-17.17, -31.14) * mm});
            skLineSegment(sketch, "E387", {"start": v(-16.95, -32.39) * mm, "end": v(-16.96, -32.38) * mm});
            skLineSegment(sketch, "E388", {"start": v(-16.96, -32.38) * mm, "end": v(-16.98, -32.37) * mm});
            skLineSegment(sketch, "E389", {"start": v(-16.98, -32.37) * mm, "end": v(-17, -32.36) * mm});
            skLineSegment(sketch, "E390", {"start": v(-17, -32.36) * mm, "end": v(-17, -32.35) * mm});
            skLineSegment(sketch, "E391", {"start": v(-17, -32.35) * mm, "end": v(-17.02, -32.33) * mm});
            skLineSegment(sketch, "E392", {"start": v(-17.02, -32.33) * mm, "end": v(-17.03, -32.32) * mm});
            skLineSegment(sketch, "E393", {"start": v(-17.03, -32.32) * mm, "end": v(-17.04, -32.3) * mm});
            skLineSegment(sketch, "E394", {"start": v(-17.04, -32.3) * mm, "end": v(-17.06, -32.3) * mm});
            skLineSegment(sketch, "E395", {"start": v(-17.06, -32.3) * mm, "end": v(-17.07, -32.28) * mm});
            skLineSegment(sketch, "E396", {"start": v(-17.07, -32.28) * mm, "end": v(-17.08, -32.27) * mm});
            skLineSegment(sketch, "E397", {"start": v(-17.08, -32.27) * mm, "end": v(-17.09, -32.25) * mm});
            skLineSegment(sketch, "E398", {"start": v(-17.09, -32.25) * mm, "end": v(-17.1, -32.24) * mm});
            skLineSegment(sketch, "E399", {"start": v(-17.1, -32.24) * mm, "end": v(-17.1, -32.22) * mm});
            skLineSegment(sketch, "E400", {"start": v(-17.1, -32.22) * mm, "end": v(-17.11, -32.2) * mm});
            skLineSegment(sketch, "E401", {"start": v(-17.11, -32.2) * mm, "end": v(-17.12, -32.2) * mm});
            skLineSegment(sketch, "E402", {"start": v(-17.12, -32.2) * mm, "end": v(-17.13, -32.17) * mm});
            skLineSegment(sketch, "E403", {"start": v(-17.13, -32.17) * mm, "end": v(-17.13, -32.16) * mm});
            skLineSegment(sketch, "E404", {"start": v(-17.13, -32.16) * mm, "end": v(-17.14, -32.14) * mm});
            skLineSegment(sketch, "E405", {"start": v(-17.14, -32.14) * mm, "end": v(-17.14, -32.12) * mm});
            skLineSegment(sketch, "E406", {"start": v(-17.14, -32.12) * mm, "end": v(-17.15, -32.1) * mm});
            skLineSegment(sketch, "E407", {"start": v(-17.15, -32.1) * mm, "end": v(-17.15, -32.09) * mm});
            skLineSegment(sketch, "E408", {"start": v(-17.15, -32.09) * mm, "end": v(-17.15, -32.07) * mm});
            skLineSegment(sketch, "E409", {"start": v(-17.15, -32.07) * mm, "end": v(-17.15, -32.05) * mm});
            skLineSegment(sketch, "E410", {"start": v(-17.15, -32.05) * mm, "end": v(-17.15, -32.04) * mm});
            skLineSegment(sketch, "E411", {"start": v(-16.25, -32.79) * mm, "end": v(-16.28, -32.77) * mm});
            skLineSegment(sketch, "E412", {"start": v(-16.28, -32.77) * mm, "end": v(-16.3, -32.76) * mm});
            skLineSegment(sketch, "E413", {"start": v(-16.3, -32.76) * mm, "end": v(-16.34, -32.74) * mm});
            skLineSegment(sketch, "E414", {"start": v(-16.34, -32.74) * mm, "end": v(-16.36, -32.72) * mm});
            skLineSegment(sketch, "E415", {"start": v(-16.36, -32.72) * mm, "end": v(-16.4, -32.7) * mm});
            skLineSegment(sketch, "E416", {"start": v(-16.4, -32.7) * mm, "end": v(-16.42, -32.69) * mm});
            skLineSegment(sketch, "E417", {"start": v(-16.42, -32.69) * mm, "end": v(-16.45, -32.67) * mm});
            skLineSegment(sketch, "E418", {"start": v(-16.45, -32.67) * mm, "end": v(-16.48, -32.66) * mm});
            skLineSegment(sketch, "E419", {"start": v(-16.48, -32.66) * mm, "end": v(-16.51, -32.64) * mm});
            skLineSegment(sketch, "E420", {"start": v(-16.51, -32.64) * mm, "end": v(-16.54, -32.62) * mm});
            skLineSegment(sketch, "E421", {"start": v(-16.54, -32.62) * mm, "end": v(-16.57, -32.6) * mm});
            skLineSegment(sketch, "E422", {"start": v(-16.57, -32.6) * mm, "end": v(-16.6, -32.59) * mm});
            skLineSegment(sketch, "E423", {"start": v(-16.6, -32.59) * mm, "end": v(-16.63, -32.57) * mm});
            skLineSegment(sketch, "E424", {"start": v(-16.63, -32.57) * mm, "end": v(-16.66, -32.55) * mm});
            skLineSegment(sketch, "E425", {"start": v(-16.66, -32.55) * mm, "end": v(-16.69, -32.54) * mm});
            skLineSegment(sketch, "E426", {"start": v(-16.69, -32.54) * mm, "end": v(-16.71, -32.52) * mm});
            skLineSegment(sketch, "E427", {"start": v(-16.71, -32.52) * mm, "end": v(-16.74, -32.5) * mm});
            skLineSegment(sketch, "E428", {"start": v(-16.74, -32.5) * mm, "end": v(-16.77, -32.49) * mm});
            skLineSegment(sketch, "E429", {"start": v(-16.77, -32.49) * mm, "end": v(-16.8, -32.47) * mm});
            skLineSegment(sketch, "E430", {"start": v(-16.8, -32.47) * mm, "end": v(-16.83, -32.45) * mm});
            skLineSegment(sketch, "E431", {"start": v(-16.83, -32.45) * mm, "end": v(-16.86, -32.44) * mm});
            skLineSegment(sketch, "E432", {"start": v(-16.86, -32.44) * mm, "end": v(-16.89, -32.42) * mm});
            skLineSegment(sketch, "E433", {"start": v(-16.89, -32.42) * mm, "end": v(-16.92, -32.4) * mm});
            skLineSegment(sketch, "E434", {"start": v(-16.92, -32.4) * mm, "end": v(-16.95, -32.39) * mm});
            skLineSegment(sketch, "E435", {"start": v(-16.04, -33.15) * mm, "end": v(-16.04, -33.13) * mm});
            skLineSegment(sketch, "E436", {"start": v(-16.04, -33.13) * mm, "end": v(-16.04, -33.11) * mm});
            skLineSegment(sketch, "E437", {"start": v(-16.04, -33.11) * mm, "end": v(-16.05, -33.1) * mm});
            skLineSegment(sketch, "E438", {"start": v(-16.05, -33.1) * mm, "end": v(-16.05, -33.07) * mm});
            skLineSegment(sketch, "E439", {"start": v(-16.05, -33.07) * mm, "end": v(-16.05, -33.06) * mm});
            skLineSegment(sketch, "E440", {"start": v(-16.05, -33.06) * mm, "end": v(-16.06, -33.04) * mm});
            skLineSegment(sketch, "E441", {"start": v(-16.06, -33.04) * mm, "end": v(-16.06, -33.02) * mm});
            skLineSegment(sketch, "E442", {"start": v(-16.06, -33.02) * mm, "end": v(-16.07, -33) * mm});
            skLineSegment(sketch, "E443", {"start": v(-16.07, -33) * mm, "end": v(-16.07, -32.99) * mm});
            skLineSegment(sketch, "E444", {"start": v(-16.07, -32.99) * mm, "end": v(-16.08, -32.97) * mm});
            skLineSegment(sketch, "E445", {"start": v(-16.08, -32.97) * mm, "end": v(-16.09, -32.96) * mm});
            skLineSegment(sketch, "E446", {"start": v(-16.09, -32.96) * mm, "end": v(-16.1, -32.94) * mm});
            skLineSegment(sketch, "E447", {"start": v(-16.1, -32.94) * mm, "end": v(-16.1, -32.93) * mm});
            skLineSegment(sketch, "E448", {"start": v(-16.1, -32.93) * mm, "end": v(-16.12, -32.91) * mm});
            skLineSegment(sketch, "E449", {"start": v(-16.12, -32.91) * mm, "end": v(-16.13, -32.9) * mm});
            skLineSegment(sketch, "E450", {"start": v(-16.13, -32.9) * mm, "end": v(-16.14, -32.88) * mm});
            skLineSegment(sketch, "E451", {"start": v(-16.14, -32.88) * mm, "end": v(-16.15, -32.87) * mm});
            skLineSegment(sketch, "E452", {"start": v(-16.15, -32.87) * mm, "end": v(-16.16, -32.86) * mm});
            skLineSegment(sketch, "E453", {"start": v(-16.16, -32.86) * mm, "end": v(-16.18, -32.84) * mm});
            skLineSegment(sketch, "E454", {"start": v(-16.18, -32.84) * mm, "end": v(-16.19, -32.83) * mm});
            skLineSegment(sketch, "E455", {"start": v(-16.19, -32.83) * mm, "end": v(-16.2, -32.82) * mm});
            skLineSegment(sketch, "E456", {"start": v(-16.2, -32.82) * mm, "end": v(-16.22, -32.8) * mm});
            skLineSegment(sketch, "E457", {"start": v(-16.22, -32.8) * mm, "end": v(-16.23, -32.8) * mm});
            skLineSegment(sketch, "E458", {"start": v(-16.23, -32.8) * mm, "end": v(-16.25, -32.79) * mm});
            skLineSegment(sketch, "E459", {"start": v(-16.04, -33.3) * mm, "end": v(-16.04, -33.28) * mm});
            skLineSegment(sketch, "E460", {"start": v(-16.04, -33.28) * mm, "end": v(-16.04, -33.28) * mm});
            skLineSegment(sketch, "E461", {"start": v(-16.04, -33.28) * mm, "end": v(-16.04, -33.27) * mm});
            skLineSegment(sketch, "E462", {"start": v(-16.04, -33.27) * mm, "end": v(-16.04, -33.27) * mm});
            skLineSegment(sketch, "E463", {"start": v(-16.04, -33.27) * mm, "end": v(-16.04, -33.26) * mm});
            skLineSegment(sketch, "E464", {"start": v(-16.04, -33.26) * mm, "end": v(-16.04, -33.25) * mm});
            skLineSegment(sketch, "E465", {"start": v(-16.04, -33.25) * mm, "end": v(-16.04, -33.25) * mm});
            skLineSegment(sketch, "E466", {"start": v(-16.04, -33.25) * mm, "end": v(-16.04, -33.24) * mm});
            skLineSegment(sketch, "E467", {"start": v(-16.04, -33.24) * mm, "end": v(-16.04, -33.24) * mm});
            skLineSegment(sketch, "E468", {"start": v(-16.04, -33.24) * mm, "end": v(-16.04, -33.23) * mm});
            skLineSegment(sketch, "E469", {"start": v(-16.04, -33.23) * mm, "end": v(-16.04, -33.22) * mm});
            skLineSegment(sketch, "E470", {"start": v(-16.04, -33.22) * mm, "end": v(-16.04, -33.22) * mm});
            skLineSegment(sketch, "E471", {"start": v(-16.04, -33.22) * mm, "end": v(-16.04, -33.21) * mm});
            skLineSegment(sketch, "E472", {"start": v(-16.04, -33.21) * mm, "end": v(-16.04, -33.2) * mm});
            skLineSegment(sketch, "E473", {"start": v(-16.04, -33.2) * mm, "end": v(-16.04, -33.2) * mm});
            skLineSegment(sketch, "E474", {"start": v(-16.04, -33.2) * mm, "end": v(-16.04, -33.19) * mm});
            skLineSegment(sketch, "E475", {"start": v(-16.04, -33.19) * mm, "end": v(-16.04, -33.18) * mm});
            skLineSegment(sketch, "E476", {"start": v(-16.04, -33.18) * mm, "end": v(-16.04, -33.18) * mm});
            skLineSegment(sketch, "E477", {"start": v(-16.04, -33.18) * mm, "end": v(-16.04, -33.17) * mm});
            skLineSegment(sketch, "E478", {"start": v(-16.04, -33.17) * mm, "end": v(-16.04, -33.16) * mm});
            skLineSegment(sketch, "E479", {"start": v(-16.04, -33.16) * mm, "end": v(-16.04, -33.16) * mm});
            skLineSegment(sketch, "E480", {"start": v(-16.04, -33.16) * mm, "end": v(-16.04, -33.15) * mm});
            skLineSegment(sketch, "E481", {"start": v(-16.04, -33.15) * mm, "end": v(-16.04, -33.15) * mm});
            skLineSegment(sketch, "E482", {"start": v(-17.13, -33.3) * mm, "end": v(-16.04, -33.3) * mm});
            skLineSegment(sketch, "E483", {"start": v(-17.1, -35.05) * mm, "end": v(-17.13, -33.3) * mm});
            skLineSegment(sketch, "E484", {"start": v(-17.1, -36.65) * mm, "end": v(-17.1, -35.05) * mm});
            skLineSegment(sketch, "E485", {"start": v(-19.55, -36.65) * mm, "end": v(-17.1, -36.65) * mm});
            skLineSegment(sketch, "E486", {"start": v(-19.55, -23.8) * mm, "end": v(-19.55, -36.65) * mm});
            skLineSegment(sketch, "E487", {"start": v(17.1, -35.05) * mm, "end": v(17.1, -36.65) * mm});
            skLineSegment(sketch, "E488", {"start": v(17.14, -32.86) * mm, "end": v(17.1, -35.05) * mm});
            skLineSegment(sketch, "E489", {"start": v(16.93, -32.5) * mm, "end": v(16.95, -32.5) * mm});
            skLineSegment(sketch, "E490", {"start": v(16.95, -32.5) * mm, "end": v(16.96, -32.51) * mm});
            skLineSegment(sketch, "E491", {"start": v(16.96, -32.51) * mm, "end": v(16.98, -32.52) * mm});
            skLineSegment(sketch, "E492", {"start": v(16.98, -32.52) * mm, "end": v(17, -32.54) * mm});
            skLineSegment(sketch, "E493", {"start": v(17, -32.54) * mm, "end": v(17, -32.55) * mm});
            skLineSegment(sketch, "E494", {"start": v(17, -32.55) * mm, "end": v(17.02, -32.56) * mm});
            skLineSegment(sketch, "E495", {"start": v(17.02, -32.56) * mm, "end": v(17.03, -32.57) * mm});
            skLineSegment(sketch, "E496", {"start": v(17.03, -32.57) * mm, "end": v(17.04, -32.59) * mm});
            skLineSegment(sketch, "E497", {"start": v(17.04, -32.59) * mm, "end": v(17.06, -32.6) * mm});
            skLineSegment(sketch, "E498", {"start": v(17.06, -32.6) * mm, "end": v(17.07, -32.62) * mm});
            skLineSegment(sketch, "E499", {"start": v(17.07, -32.62) * mm, "end": v(17.08, -32.63) * mm});
            skLineSegment(sketch, "E500", {"start": v(17.08, -32.63) * mm, "end": v(17.09, -32.65) * mm});
            skLineSegment(sketch, "E501", {"start": v(17.09, -32.65) * mm, "end": v(17.1, -32.66) * mm});
            skLineSegment(sketch, "E502", {"start": v(17.1, -32.66) * mm, "end": v(17.1, -32.68) * mm});
            skLineSegment(sketch, "E503", {"start": v(17.1, -32.68) * mm, "end": v(17.1, -32.7) * mm});
            skLineSegment(sketch, "E504", {"start": v(17.1, -32.7) * mm, "end": v(17.12, -32.71) * mm});
            skLineSegment(sketch, "E505", {"start": v(17.12, -32.71) * mm, "end": v(17.12, -32.73) * mm});
            skLineSegment(sketch, "E506", {"start": v(17.12, -32.73) * mm, "end": v(17.13, -32.75) * mm});
            skLineSegment(sketch, "E507", {"start": v(17.13, -32.75) * mm, "end": v(17.13, -32.77) * mm});
            skLineSegment(sketch, "E508", {"start": v(17.13, -32.77) * mm, "end": v(17.13, -32.78) * mm});
            skLineSegment(sketch, "E509", {"start": v(17.13, -32.78) * mm, "end": v(17.14, -32.8) * mm});
            skLineSegment(sketch, "E510", {"start": v(17.14, -32.8) * mm, "end": v(17.14, -32.82) * mm});
            skLineSegment(sketch, "E511", {"start": v(17.14, -32.82) * mm, "end": v(17.14, -32.84) * mm});
            skLineSegment(sketch, "E512", {"start": v(17.14, -32.84) * mm, "end": v(17.14, -32.86) * mm});
            skLineSegment(sketch, "E513", {"start": v(16.28, -32.12) * mm, "end": v(16.3, -32.13) * mm});
            skLineSegment(sketch, "E514", {"start": v(16.3, -32.13) * mm, "end": v(16.33, -32.15) * mm});
            skLineSegment(sketch, "E515", {"start": v(16.33, -32.15) * mm, "end": v(16.36, -32.16) * mm});
            skLineSegment(sketch, "E516", {"start": v(16.36, -32.16) * mm, "end": v(16.39, -32.18) * mm});
            skLineSegment(sketch, "E517", {"start": v(16.39, -32.18) * mm, "end": v(16.41, -32.2) * mm});
            skLineSegment(sketch, "E518", {"start": v(16.41, -32.2) * mm, "end": v(16.44, -32.2) * mm});
            skLineSegment(sketch, "E519", {"start": v(16.44, -32.2) * mm, "end": v(16.47, -32.23) * mm});
            skLineSegment(sketch, "E520", {"start": v(16.47, -32.23) * mm, "end": v(16.5, -32.24) * mm});
            skLineSegment(sketch, "E521", {"start": v(16.5, -32.24) * mm, "end": v(16.52, -32.26) * mm});
            skLineSegment(sketch, "E522", {"start": v(16.52, -32.26) * mm, "end": v(16.55, -32.27) * mm});
            skLineSegment(sketch, "E523", {"start": v(16.55, -32.27) * mm, "end": v(16.58, -32.29) * mm});
            skLineSegment(sketch, "E524", {"start": v(16.58, -32.29) * mm, "end": v(16.6, -32.3) * mm});
            skLineSegment(sketch, "E525", {"start": v(16.6, -32.3) * mm, "end": v(16.63, -32.32) * mm});
            skLineSegment(sketch, "E526", {"start": v(16.63, -32.32) * mm, "end": v(16.66, -32.34) * mm});
            skLineSegment(sketch, "E527", {"start": v(16.66, -32.34) * mm, "end": v(16.69, -32.35) * mm});
            skLineSegment(sketch, "E528", {"start": v(16.69, -32.35) * mm, "end": v(16.71, -32.37) * mm});
            skLineSegment(sketch, "E529", {"start": v(16.71, -32.37) * mm, "end": v(16.74, -32.38) * mm});
            skLineSegment(sketch, "E530", {"start": v(16.74, -32.38) * mm, "end": v(16.77, -32.4) * mm});
            skLineSegment(sketch, "E531", {"start": v(16.77, -32.4) * mm, "end": v(16.8, -32.41) * mm});
            skLineSegment(sketch, "E532", {"start": v(16.8, -32.41) * mm, "end": v(16.82, -32.43) * mm});
            skLineSegment(sketch, "E533", {"start": v(16.82, -32.43) * mm, "end": v(16.85, -32.45) * mm});
            skLineSegment(sketch, "E534", {"start": v(16.85, -32.45) * mm, "end": v(16.88, -32.46) * mm});
            skLineSegment(sketch, "E535", {"start": v(16.88, -32.46) * mm, "end": v(16.9, -32.48) * mm});
            skLineSegment(sketch, "E536", {"start": v(16.9, -32.48) * mm, "end": v(16.93, -32.5) * mm});
            skLineSegment(sketch, "E537", {"start": v(16.07, -31.76) * mm, "end": v(16.07, -31.78) * mm});
            skLineSegment(sketch, "E538", {"start": v(16.07, -31.78) * mm, "end": v(16.07, -31.8) * mm});
            skLineSegment(sketch, "E539", {"start": v(16.07, -31.8) * mm, "end": v(16.08, -31.81) * mm});
            skLineSegment(sketch, "E540", {"start": v(16.08, -31.81) * mm, "end": v(16.08, -31.83) * mm});
            skLineSegment(sketch, "E541", {"start": v(16.08, -31.83) * mm, "end": v(16.08, -31.85) * mm});
            skLineSegment(sketch, "E542", {"start": v(16.08, -31.85) * mm, "end": v(16.09, -31.87) * mm});
            skLineSegment(sketch, "E543", {"start": v(16.09, -31.87) * mm, "end": v(16.1, -31.88) * mm});
            skLineSegment(sketch, "E544", {"start": v(16.1, -31.88) * mm, "end": v(16.1, -31.9) * mm});
            skLineSegment(sketch, "E545", {"start": v(16.1, -31.9) * mm, "end": v(16.1, -31.92) * mm});
            skLineSegment(sketch, "E546", {"start": v(16.1, -31.92) * mm, "end": v(16.11, -31.93) * mm});
            skLineSegment(sketch, "E547", {"start": v(16.11, -31.93) * mm, "end": v(16.12, -31.95) * mm});
            skLineSegment(sketch, "E548", {"start": v(16.12, -31.95) * mm, "end": v(16.13, -31.96) * mm});
            skLineSegment(sketch, "E549", {"start": v(16.13, -31.96) * mm, "end": v(16.14, -31.98) * mm});
            skLineSegment(sketch, "E550", {"start": v(16.14, -31.98) * mm, "end": v(16.15, -32) * mm});
            skLineSegment(sketch, "E551", {"start": v(16.15, -32) * mm, "end": v(16.16, -32) * mm});
            skLineSegment(sketch, "E552", {"start": v(16.16, -32) * mm, "end": v(16.17, -32.02) * mm});
            skLineSegment(sketch, "E553", {"start": v(16.17, -32.02) * mm, "end": v(16.18, -32.04) * mm});
            skLineSegment(sketch, "E554", {"start": v(16.18, -32.04) * mm, "end": v(16.2, -32.05) * mm});
            skLineSegment(sketch, "E555", {"start": v(16.2, -32.05) * mm, "end": v(16.2, -32.06) * mm});
            skLineSegment(sketch, "E556", {"start": v(16.2, -32.06) * mm, "end": v(16.22, -32.07) * mm});
            skLineSegment(sketch, "E557", {"start": v(16.22, -32.07) * mm, "end": v(16.23, -32.09) * mm});
            skLineSegment(sketch, "E558", {"start": v(16.23, -32.09) * mm, "end": v(16.25, -32.1) * mm});
            skLineSegment(sketch, "E559", {"start": v(16.25, -32.1) * mm, "end": v(16.26, -32.1) * mm});
            skLineSegment(sketch, "E560", {"start": v(16.26, -32.1) * mm, "end": v(16.28, -32.12) * mm});
            skLineSegment(sketch, "E561", {"start": v(16.07, -31.6) * mm, "end": v(16.07, -31.6) * mm});
            skLineSegment(sketch, "E562", {"start": v(16.07, -31.6) * mm, "end": v(16.07, -31.62) * mm});
            skLineSegment(sketch, "E563", {"start": v(16.07, -31.62) * mm, "end": v(16.07, -31.62) * mm});
            skLineSegment(sketch, "E564", {"start": v(16.07, -31.62) * mm, "end": v(16.07, -31.63) * mm});
            skLineSegment(sketch, "E565", {"start": v(16.07, -31.63) * mm, "end": v(16.07, -31.64) * mm});
            skLineSegment(sketch, "E566", {"start": v(16.07, -31.64) * mm, "end": v(16.07, -31.64) * mm});
            skLineSegment(sketch, "E567", {"start": v(16.07, -31.64) * mm, "end": v(16.07, -31.65) * mm});
            skLineSegment(sketch, "E568", {"start": v(16.07, -31.65) * mm, "end": v(16.07, -31.66) * mm});
            skLineSegment(sketch, "E569", {"start": v(16.07, -31.66) * mm, "end": v(16.07, -31.66) * mm});
            skLineSegment(sketch, "E570", {"start": v(16.07, -31.66) * mm, "end": v(16.07, -31.67) * mm});
            skLineSegment(sketch, "E571", {"start": v(16.07, -31.67) * mm, "end": v(16.07, -31.68) * mm});
            skLineSegment(sketch, "E572", {"start": v(16.07, -31.68) * mm, "end": v(16.07, -31.68) * mm});
            skLineSegment(sketch, "E573", {"start": v(16.07, -31.68) * mm, "end": v(16.07, -31.7) * mm});
            skLineSegment(sketch, "E574", {"start": v(16.07, -31.7) * mm, "end": v(16.07, -31.7) * mm});
            skLineSegment(sketch, "E575", {"start": v(16.07, -31.7) * mm, "end": v(16.07, -31.71) * mm});
            skLineSegment(sketch, "E576", {"start": v(16.07, -31.71) * mm, "end": v(16.07, -31.72) * mm});
            skLineSegment(sketch, "E577", {"start": v(16.07, -31.72) * mm, "end": v(16.07, -31.72) * mm});
            skLineSegment(sketch, "E578", {"start": v(16.07, -31.72) * mm, "end": v(16.07, -31.73) * mm});
            skLineSegment(sketch, "E579", {"start": v(16.07, -31.73) * mm, "end": v(16.07, -31.74) * mm});
            skLineSegment(sketch, "E580", {"start": v(16.07, -31.74) * mm, "end": v(16.07, -31.75) * mm});
            skLineSegment(sketch, "E581", {"start": v(16.07, -31.75) * mm, "end": v(16.07, -31.75) * mm});
            skLineSegment(sketch, "E582", {"start": v(16.07, -31.75) * mm, "end": v(16.07, -31.76) * mm});
            skLineSegment(sketch, "E583", {"start": v(16.07, -31.43) * mm, "end": v(16.07, -31.44) * mm});
            skLineSegment(sketch, "E584", {"start": v(16.07, -31.44) * mm, "end": v(16.07, -31.45) * mm});
            skLineSegment(sketch, "E585", {"start": v(16.07, -31.45) * mm, "end": v(16.07, -31.45) * mm});
            skLineSegment(sketch, "E586", {"start": v(16.07, -31.45) * mm, "end": v(16.07, -31.46) * mm});
            skLineSegment(sketch, "E587", {"start": v(16.07, -31.46) * mm, "end": v(16.07, -31.47) * mm});
            skLineSegment(sketch, "E588", {"start": v(16.07, -31.47) * mm, "end": v(16.07, -31.47) * mm});
            skLineSegment(sketch, "E589", {"start": v(16.07, -31.47) * mm, "end": v(16.07, -31.48) * mm});
            skLineSegment(sketch, "E590", {"start": v(16.07, -31.48) * mm, "end": v(16.07, -31.49) * mm});
            skLineSegment(sketch, "E591", {"start": v(16.07, -31.49) * mm, "end": v(16.07, -31.5) * mm});
            skLineSegment(sketch, "E592", {"start": v(16.07, -31.5) * mm, "end": v(16.07, -31.5) * mm});
            skLineSegment(sketch, "E593", {"start": v(16.07, -31.5) * mm, "end": v(16.07, -31.51) * mm});
            skLineSegment(sketch, "E594", {"start": v(16.07, -31.51) * mm, "end": v(16.07, -31.52) * mm});
            skLineSegment(sketch, "E595", {"start": v(16.07, -31.52) * mm, "end": v(16.07, -31.53) * mm});
            skLineSegment(sketch, "E596", {"start": v(16.07, -31.53) * mm, "end": v(16.07, -31.53) * mm});
            skLineSegment(sketch, "E597", {"start": v(16.07, -31.53) * mm, "end": v(16.07, -31.54) * mm});
            skLineSegment(sketch, "E598", {"start": v(16.07, -31.54) * mm, "end": v(16.07, -31.55) * mm});
            skLineSegment(sketch, "E599", {"start": v(16.07, -31.55) * mm, "end": v(16.07, -31.55) * mm});
            skLineSegment(sketch, "E600", {"start": v(16.07, -31.55) * mm, "end": v(16.07, -31.56) * mm});
            skLineSegment(sketch, "E601", {"start": v(16.07, -31.56) * mm, "end": v(16.07, -31.57) * mm});
            skLineSegment(sketch, "E602", {"start": v(16.07, -31.57) * mm, "end": v(16.07, -31.57) * mm});
            skLineSegment(sketch, "E603", {"start": v(16.07, -31.57) * mm, "end": v(16.07, -31.58) * mm});
            skLineSegment(sketch, "E604", {"start": v(16.07, -31.58) * mm, "end": v(16.07, -31.59) * mm});
            skLineSegment(sketch, "E605", {"start": v(16.07, -31.59) * mm, "end": v(16.07, -31.6) * mm});
            skLineSegment(sketch, "E606", {"start": v(16.28, -31.08) * mm, "end": v(16.26, -31.08) * mm});
            skLineSegment(sketch, "E607", {"start": v(16.26, -31.08) * mm, "end": v(16.25, -31.1) * mm});
            skLineSegment(sketch, "E608", {"start": v(16.25, -31.1) * mm, "end": v(16.23, -31.1) * mm});
            skLineSegment(sketch, "E609", {"start": v(16.23, -31.1) * mm, "end": v(16.22, -31.12) * mm});
            skLineSegment(sketch, "E610", {"start": v(16.22, -31.12) * mm, "end": v(16.2, -31.13) * mm});
            skLineSegment(sketch, "E611", {"start": v(16.2, -31.13) * mm, "end": v(16.2, -31.14) * mm});
            skLineSegment(sketch, "E612", {"start": v(16.2, -31.14) * mm, "end": v(16.18, -31.15) * mm});
            skLineSegment(sketch, "E613", {"start": v(16.18, -31.15) * mm, "end": v(16.17, -31.17) * mm});
            skLineSegment(sketch, "E614", {"start": v(16.17, -31.17) * mm, "end": v(16.16, -31.18) * mm});
            skLineSegment(sketch, "E615", {"start": v(16.16, -31.18) * mm, "end": v(16.15, -31.2) * mm});
            skLineSegment(sketch, "E616", {"start": v(16.15, -31.2) * mm, "end": v(16.14, -31.21) * mm});
            skLineSegment(sketch, "E617", {"start": v(16.14, -31.21) * mm, "end": v(16.13, -31.23) * mm});
            skLineSegment(sketch, "E618", {"start": v(16.13, -31.23) * mm, "end": v(16.12, -31.24) * mm});
            skLineSegment(sketch, "E619", {"start": v(16.12, -31.24) * mm, "end": v(16.11, -31.26) * mm});
            skLineSegment(sketch, "E620", {"start": v(16.11, -31.26) * mm, "end": v(16.1, -31.27) * mm});
            skLineSegment(sketch, "E621", {"start": v(16.1, -31.27) * mm, "end": v(16.1, -31.3) * mm});
            skLineSegment(sketch, "E622", {"start": v(16.1, -31.3) * mm, "end": v(16.1, -31.3) * mm});
            skLineSegment(sketch, "E623", {"start": v(16.1, -31.3) * mm, "end": v(16.09, -31.33) * mm});
            skLineSegment(sketch, "E624", {"start": v(16.09, -31.33) * mm, "end": v(16.08, -31.34) * mm});
            skLineSegment(sketch, "E625", {"start": v(16.08, -31.34) * mm, "end": v(16.08, -31.36) * mm});
            skLineSegment(sketch, "E626", {"start": v(16.08, -31.36) * mm, "end": v(16.08, -31.38) * mm});
            skLineSegment(sketch, "E627", {"start": v(16.08, -31.38) * mm, "end": v(16.07, -31.4) * mm});
            skLineSegment(sketch, "E628", {"start": v(16.07, -31.4) * mm, "end": v(16.07, -31.41) * mm});
            skLineSegment(sketch, "E629", {"start": v(16.07, -31.41) * mm, "end": v(16.07, -31.43) * mm});
            skLineSegment(sketch, "E630", {"start": v(16.98, -30.67) * mm, "end": v(16.95, -30.69) * mm});
            skLineSegment(sketch, "E631", {"start": v(16.95, -30.69) * mm, "end": v(16.92, -30.7) * mm});
            skLineSegment(sketch, "E632", {"start": v(16.92, -30.7) * mm, "end": v(16.9, -30.72) * mm});
            skLineSegment(sketch, "E633", {"start": v(16.9, -30.72) * mm, "end": v(16.86, -30.74) * mm});
            skLineSegment(sketch, "E634", {"start": v(16.86, -30.74) * mm, "end": v(16.83, -30.76) * mm});
            skLineSegment(sketch, "E635", {"start": v(16.83, -30.76) * mm, "end": v(16.8, -30.77) * mm});
            skLineSegment(sketch, "E636", {"start": v(16.8, -30.77) * mm, "end": v(16.77, -30.79) * mm});
            skLineSegment(sketch, "E637", {"start": v(16.77, -30.79) * mm, "end": v(16.74, -30.8) * mm});
            skLineSegment(sketch, "E638", {"start": v(16.74, -30.8) * mm, "end": v(16.72, -30.82) * mm});
            skLineSegment(sketch, "E639", {"start": v(16.72, -30.82) * mm, "end": v(16.69, -30.84) * mm});
            skLineSegment(sketch, "E640", {"start": v(16.69, -30.84) * mm, "end": v(16.66, -30.86) * mm});
            skLineSegment(sketch, "E641", {"start": v(16.66, -30.86) * mm, "end": v(16.63, -30.87) * mm});
            skLineSegment(sketch, "E642", {"start": v(16.63, -30.87) * mm, "end": v(16.6, -30.9) * mm});
            skLineSegment(sketch, "E643", {"start": v(16.6, -30.9) * mm, "end": v(16.57, -30.9) * mm});
            skLineSegment(sketch, "E644", {"start": v(16.57, -30.9) * mm, "end": v(16.54, -30.92) * mm});
            skLineSegment(sketch, "E645", {"start": v(16.54, -30.92) * mm, "end": v(16.51, -30.94) * mm});
            skLineSegment(sketch, "E646", {"start": v(16.51, -30.94) * mm, "end": v(16.48, -30.96) * mm});
            skLineSegment(sketch, "E647", {"start": v(16.48, -30.96) * mm, "end": v(16.45, -30.97) * mm});
            skLineSegment(sketch, "E648", {"start": v(16.45, -30.97) * mm, "end": v(16.42, -31) * mm});
            skLineSegment(sketch, "E649", {"start": v(16.42, -31) * mm, "end": v(16.4, -31) * mm});
            skLineSegment(sketch, "E650", {"start": v(16.4, -31) * mm, "end": v(16.37, -31.02) * mm});
            skLineSegment(sketch, "E651", {"start": v(16.37, -31.02) * mm, "end": v(16.34, -31.04) * mm});
            skLineSegment(sketch, "E652", {"start": v(16.34, -31.04) * mm, "end": v(16.3, -31.06) * mm});
            skLineSegment(sketch, "E653", {"start": v(16.3, -31.06) * mm, "end": v(16.28, -31.08) * mm});
            skLineSegment(sketch, "E654", {"start": v(17.18, -30.32) * mm, "end": v(17.18, -30.34) * mm});
            skLineSegment(sketch, "E655", {"start": v(17.18, -30.34) * mm, "end": v(17.18, -30.36) * mm});
            skLineSegment(sketch, "E656", {"start": v(17.18, -30.36) * mm, "end": v(17.18, -30.37) * mm});
            skLineSegment(sketch, "E657", {"start": v(17.18, -30.37) * mm, "end": v(17.18, -30.4) * mm});
            skLineSegment(sketch, "E658", {"start": v(17.18, -30.4) * mm, "end": v(17.17, -30.4) * mm});
            skLineSegment(sketch, "E659", {"start": v(17.17, -30.4) * mm, "end": v(17.17, -30.43) * mm});
            skLineSegment(sketch, "E660", {"start": v(17.17, -30.43) * mm, "end": v(17.16, -30.44) * mm});
            skLineSegment(sketch, "E661", {"start": v(17.16, -30.44) * mm, "end": v(17.16, -30.46) * mm});
            skLineSegment(sketch, "E662", {"start": v(17.16, -30.46) * mm, "end": v(17.15, -30.48) * mm});
            skLineSegment(sketch, "E663", {"start": v(17.15, -30.48) * mm, "end": v(17.14, -30.5) * mm});
            skLineSegment(sketch, "E664", {"start": v(17.14, -30.5) * mm, "end": v(17.14, -30.5) * mm});
            skLineSegment(sketch, "E665", {"start": v(17.14, -30.5) * mm, "end": v(17.13, -30.52) * mm});
            skLineSegment(sketch, "E666", {"start": v(17.13, -30.52) * mm, "end": v(17.12, -30.54) * mm});
            skLineSegment(sketch, "E667", {"start": v(17.12, -30.54) * mm, "end": v(17.1, -30.55) * mm});
            skLineSegment(sketch, "E668", {"start": v(17.1, -30.55) * mm, "end": v(17.1, -30.57) * mm});
            skLineSegment(sketch, "E669", {"start": v(17.1, -30.57) * mm, "end": v(17.09, -30.58) * mm});
            skLineSegment(sketch, "E670", {"start": v(17.09, -30.58) * mm, "end": v(17.07, -30.6) * mm});
            skLineSegment(sketch, "E671", {"start": v(17.07, -30.6) * mm, "end": v(17.06, -30.6) * mm});
            skLineSegment(sketch, "E672", {"start": v(17.06, -30.6) * mm, "end": v(17.05, -30.62) * mm});
            skLineSegment(sketch, "E673", {"start": v(17.05, -30.62) * mm, "end": v(17.04, -30.63) * mm});
            skLineSegment(sketch, "E674", {"start": v(17.04, -30.63) * mm, "end": v(17.02, -30.64) * mm});
            skLineSegment(sketch, "E675", {"start": v(17.02, -30.64) * mm, "end": v(17, -30.65) * mm});
            skLineSegment(sketch, "E676", {"start": v(17, -30.65) * mm, "end": v(17, -30.66) * mm});
            skLineSegment(sketch, "E677", {"start": v(17, -30.66) * mm, "end": v(16.98, -30.67) * mm});
            skLineSegment(sketch, "E678", {"start": v(17.2, -29.43) * mm, "end": v(17.18, -30.32) * mm});
            skLineSegment(sketch, "E679", {"start": v(17, -29.06) * mm, "end": v(17, -29.07) * mm});
            skLineSegment(sketch, "E680", {"start": v(17, -29.07) * mm, "end": v(17.02, -29.08) * mm});
            skLineSegment(sketch, "E681", {"start": v(17.02, -29.08) * mm, "end": v(17.04, -29.1) * mm});
            skLineSegment(sketch, "E682", {"start": v(17.04, -29.1) * mm, "end": v(17.05, -29.1) * mm});
            skLineSegment(sketch, "E683", {"start": v(17.05, -29.1) * mm, "end": v(17.07, -29.12) * mm});
            skLineSegment(sketch, "E684", {"start": v(17.07, -29.12) * mm, "end": v(17.08, -29.13) * mm});
            skLineSegment(sketch, "E685", {"start": v(17.08, -29.13) * mm, "end": v(17.1, -29.14) * mm});
            skLineSegment(sketch, "E686", {"start": v(17.1, -29.14) * mm, "end": v(17.1, -29.16) * mm});
            skLineSegment(sketch, "E687", {"start": v(17.1, -29.16) * mm, "end": v(17.12, -29.17) * mm});
            skLineSegment(sketch, "E688", {"start": v(17.12, -29.17) * mm, "end": v(17.13, -29.19) * mm});
            skLineSegment(sketch, "E689", {"start": v(17.13, -29.19) * mm, "end": v(17.14, -29.2) * mm});
            skLineSegment(sketch, "E690", {"start": v(17.14, -29.2) * mm, "end": v(17.15, -29.22) * mm});
            skLineSegment(sketch, "E691", {"start": v(17.15, -29.22) * mm, "end": v(17.15, -29.23) * mm});
            skLineSegment(sketch, "E692", {"start": v(17.15, -29.23) * mm, "end": v(17.16, -29.25) * mm});
            skLineSegment(sketch, "E693", {"start": v(17.16, -29.25) * mm, "end": v(17.17, -29.27) * mm});
            skLineSegment(sketch, "E694", {"start": v(17.17, -29.27) * mm, "end": v(17.18, -29.28) * mm});
            skLineSegment(sketch, "E695", {"start": v(17.18, -29.28) * mm, "end": v(17.18, -29.3) * mm});
            skLineSegment(sketch, "E696", {"start": v(17.18, -29.3) * mm, "end": v(17.19, -29.32) * mm});
            skLineSegment(sketch, "E697", {"start": v(17.19, -29.32) * mm, "end": v(17.2, -29.34) * mm});
            skLineSegment(sketch, "E698", {"start": v(17.2, -29.34) * mm, "end": v(17.2, -29.36) * mm});
            skLineSegment(sketch, "E699", {"start": v(17.2, -29.36) * mm, "end": v(17.2, -29.37) * mm});
            skLineSegment(sketch, "E700", {"start": v(17.2, -29.37) * mm, "end": v(17.2, -29.4) * mm});
            skLineSegment(sketch, "E701", {"start": v(17.2, -29.4) * mm, "end": v(17.2, -29.4) * mm});
            skLineSegment(sketch, "E702", {"start": v(17.2, -29.4) * mm, "end": v(17.2, -29.43) * mm});
            skLineSegment(sketch, "E703", {"start": v(16.34, -28.69) * mm, "end": v(16.37, -28.7) * mm});
            skLineSegment(sketch, "E704", {"start": v(16.37, -28.7) * mm, "end": v(16.4, -28.72) * mm});
            skLineSegment(sketch, "E705", {"start": v(16.4, -28.72) * mm, "end": v(16.42, -28.73) * mm});
            skLineSegment(sketch, "E706", {"start": v(16.42, -28.73) * mm, "end": v(16.45, -28.75) * mm});
            skLineSegment(sketch, "E707", {"start": v(16.45, -28.75) * mm, "end": v(16.48, -28.76) * mm});
            skLineSegment(sketch, "E708", {"start": v(16.48, -28.76) * mm, "end": v(16.5, -28.78) * mm});
            skLineSegment(sketch, "E709", {"start": v(16.5, -28.78) * mm, "end": v(16.53, -28.8) * mm});
            skLineSegment(sketch, "E710", {"start": v(16.53, -28.8) * mm, "end": v(16.56, -28.81) * mm});
            skLineSegment(sketch, "E711", {"start": v(16.56, -28.81) * mm, "end": v(16.58, -28.83) * mm});
            skLineSegment(sketch, "E712", {"start": v(16.58, -28.83) * mm, "end": v(16.61, -28.84) * mm});
            skLineSegment(sketch, "E713", {"start": v(16.61, -28.84) * mm, "end": v(16.64, -28.86) * mm});
            skLineSegment(sketch, "E714", {"start": v(16.64, -28.86) * mm, "end": v(16.67, -28.87) * mm});
            skLineSegment(sketch, "E715", {"start": v(16.67, -28.87) * mm, "end": v(16.7, -28.9) * mm});
            skLineSegment(sketch, "E716", {"start": v(16.7, -28.9) * mm, "end": v(16.72, -28.9) * mm});
            skLineSegment(sketch, "E717", {"start": v(16.72, -28.9) * mm, "end": v(16.75, -28.92) * mm});
            skLineSegment(sketch, "E718", {"start": v(16.75, -28.92) * mm, "end": v(16.78, -28.94) * mm});
            skLineSegment(sketch, "E719", {"start": v(16.78, -28.94) * mm, "end": v(16.8, -28.95) * mm});
            skLineSegment(sketch, "E720", {"start": v(16.8, -28.95) * mm, "end": v(16.83, -28.97) * mm});
            skLineSegment(sketch, "E721", {"start": v(16.83, -28.97) * mm, "end": v(16.86, -28.99) * mm});
            skLineSegment(sketch, "E722", {"start": v(16.86, -28.99) * mm, "end": v(16.88, -29) * mm});
            skLineSegment(sketch, "E723", {"start": v(16.88, -29) * mm, "end": v(16.91, -29.02) * mm});
            skLineSegment(sketch, "E724", {"start": v(16.91, -29.02) * mm, "end": v(16.94, -29.03) * mm});
            skLineSegment(sketch, "E725", {"start": v(16.94, -29.03) * mm, "end": v(16.97, -29.05) * mm});
            skLineSegment(sketch, "E726", {"start": v(16.97, -29.05) * mm, "end": v(17, -29.06) * mm});
            skLineSegment(sketch, "E727", {"start": v(16.22, -28.58) * mm, "end": v(16.22, -28.59) * mm});
            skLineSegment(sketch, "E728", {"start": v(16.22, -28.59) * mm, "end": v(16.23, -28.6) * mm});
            skLineSegment(sketch, "E729", {"start": v(16.23, -28.6) * mm, "end": v(16.23, -28.6) * mm});
            skLineSegment(sketch, "E730", {"start": v(16.23, -28.6) * mm, "end": v(16.24, -28.6) * mm});
            skLineSegment(sketch, "E731", {"start": v(16.24, -28.6) * mm, "end": v(16.24, -28.6) * mm});
            skLineSegment(sketch, "E732", {"start": v(16.24, -28.6) * mm, "end": v(16.24, -28.61) * mm});
            skLineSegment(sketch, "E733", {"start": v(16.24, -28.61) * mm, "end": v(16.25, -28.62) * mm});
            skLineSegment(sketch, "E734", {"start": v(16.25, -28.62) * mm, "end": v(16.25, -28.62) * mm});
            skLineSegment(sketch, "E735", {"start": v(16.25, -28.62) * mm, "end": v(16.26, -28.63) * mm});
            skLineSegment(sketch, "E736", {"start": v(16.26, -28.63) * mm, "end": v(16.26, -28.63) * mm});
            skLineSegment(sketch, "E737", {"start": v(16.26, -28.63) * mm, "end": v(16.27, -28.63) * mm});
            skLineSegment(sketch, "E738", {"start": v(16.27, -28.63) * mm, "end": v(16.27, -28.64) * mm});
            skLineSegment(sketch, "E739", {"start": v(16.27, -28.64) * mm, "end": v(16.28, -28.64) * mm});
            skLineSegment(sketch, "E740", {"start": v(16.28, -28.64) * mm, "end": v(16.28, -28.65) * mm});
            skLineSegment(sketch, "E741", {"start": v(16.28, -28.65) * mm, "end": v(16.29, -28.65) * mm});
            skLineSegment(sketch, "E742", {"start": v(16.29, -28.65) * mm, "end": v(16.3, -28.66) * mm});
            skLineSegment(sketch, "E743", {"start": v(16.3, -28.66) * mm, "end": v(16.3, -28.66) * mm});
            skLineSegment(sketch, "E744", {"start": v(16.3, -28.66) * mm, "end": v(16.31, -28.67) * mm});
            skLineSegment(sketch, "E745", {"start": v(16.31, -28.67) * mm, "end": v(16.32, -28.67) * mm});
            skLineSegment(sketch, "E746", {"start": v(16.32, -28.67) * mm, "end": v(16.32, -28.68) * mm});
            skLineSegment(sketch, "E747", {"start": v(16.32, -28.68) * mm, "end": v(16.33, -28.68) * mm});
            skLineSegment(sketch, "E748", {"start": v(16.33, -28.68) * mm, "end": v(16.33, -28.68) * mm});
            skLineSegment(sketch, "E749", {"start": v(16.33, -28.68) * mm, "end": v(16.34, -28.69) * mm});
            skLineSegment(sketch, "E750", {"start": v(16.22, -28.58) * mm, "end": v(16.22, -28.54) * mm});
            skLineSegment(sketch, "E751", {"start": v(16.22, -28.54) * mm, "end": v(16.22, -28.5) * mm});
            skLineSegment(sketch, "E752", {"start": v(16.22, -28.5) * mm, "end": v(16.22, -28.47) * mm});
            skLineSegment(sketch, "E753", {"start": v(16.22, -28.47) * mm, "end": v(16.22, -28.44) * mm});
            skLineSegment(sketch, "E754", {"start": v(16.22, -28.44) * mm, "end": v(16.22, -28.4) * mm});
            skLineSegment(sketch, "E755", {"start": v(16.22, -28.4) * mm, "end": v(16.22, -28.37) * mm});
            skLineSegment(sketch, "E756", {"start": v(16.22, -28.37) * mm, "end": v(16.22, -28.33) * mm});
            skLineSegment(sketch, "E757", {"start": v(16.22, -28.33) * mm, "end": v(16.22, -28.3) * mm});
            skLineSegment(sketch, "E758", {"start": v(16.22, -28.3) * mm, "end": v(16.22, -28.26) * mm});
            skLineSegment(sketch, "E759", {"start": v(16.22, -28.26) * mm, "end": v(16.22, -28.23) * mm});
            skLineSegment(sketch, "E760", {"start": v(16.22, -28.23) * mm, "end": v(16.22, -28.2) * mm});
            skLineSegment(sketch, "E761", {"start": v(16.22, -28.2) * mm, "end": v(16.23, -28.16) * mm});
            skLineSegment(sketch, "E762", {"start": v(16.23, -28.16) * mm, "end": v(16.23, -28.12) * mm});
            skLineSegment(sketch, "E763", {"start": v(16.23, -28.12) * mm, "end": v(16.23, -28.09) * mm});
            skLineSegment(sketch, "E764", {"start": v(16.23, -28.09) * mm, "end": v(16.23, -28.05) * mm});
            skLineSegment(sketch, "E765", {"start": v(16.23, -28.05) * mm, "end": v(16.23, -28.02) * mm});
            skLineSegment(sketch, "E766", {"start": v(16.23, -28.02) * mm, "end": v(16.23, -27.98) * mm});
            skLineSegment(sketch, "E767", {"start": v(16.23, -27.98) * mm, "end": v(16.23, -27.94) * mm});
            skLineSegment(sketch, "E768", {"start": v(16.23, -27.94) * mm, "end": v(16.23, -27.9) * mm});
            skLineSegment(sketch, "E769", {"start": v(16.23, -27.9) * mm, "end": v(16.23, -27.87) * mm});
            skLineSegment(sketch, "E770", {"start": v(16.23, -27.87) * mm, "end": v(16.23, -27.84) * mm});
            skLineSegment(sketch, "E771", {"start": v(16.23, -27.84) * mm, "end": v(16.23, -27.8) * mm});
            skLineSegment(sketch, "E772", {"start": v(16.23, -27.8) * mm, "end": v(16.23, -27.77) * mm});
            skLineSegment(sketch, "E773", {"start": v(16.23, -27.77) * mm, "end": v(16.23, -27.73) * mm});
            skLineSegment(sketch, "E774", {"start": v(16.34, -27.65) * mm, "end": v(16.33, -27.65) * mm});
            skLineSegment(sketch, "E775", {"start": v(16.33, -27.65) * mm, "end": v(16.32, -27.65) * mm});
            skLineSegment(sketch, "E776", {"start": v(16.32, -27.65) * mm, "end": v(16.32, -27.66) * mm});
            skLineSegment(sketch, "E777", {"start": v(16.32, -27.66) * mm, "end": v(16.31, -27.66) * mm});
            skLineSegment(sketch, "E778", {"start": v(16.31, -27.66) * mm, "end": v(16.3, -27.66) * mm});
            skLineSegment(sketch, "E779", {"start": v(16.3, -27.66) * mm, "end": v(16.3, -27.67) * mm});
            skLineSegment(sketch, "E780", {"start": v(16.3, -27.67) * mm, "end": v(16.3, -27.68) * mm});
            skLineSegment(sketch, "E781", {"start": v(16.3, -27.68) * mm, "end": v(16.29, -27.68) * mm});
            skLineSegment(sketch, "E782", {"start": v(16.29, -27.68) * mm, "end": v(16.28, -27.69) * mm});
            skLineSegment(sketch, "E783", {"start": v(16.28, -27.69) * mm, "end": v(16.28, -27.69) * mm});
            skLineSegment(sketch, "E784", {"start": v(16.28, -27.69) * mm, "end": v(16.27, -27.7) * mm});
            skLineSegment(sketch, "E785", {"start": v(16.27, -27.7) * mm, "end": v(16.26, -27.7) * mm});
            skLineSegment(sketch, "E786", {"start": v(16.26, -27.7) * mm, "end": v(16.25, -27.71) * mm});
            skLineSegment(sketch, "E787", {"start": v(16.25, -27.71) * mm, "end": v(16.25, -27.72) * mm});
            skLineSegment(sketch, "E788", {"start": v(16.25, -27.72) * mm, "end": v(16.24, -27.72) * mm});
            skLineSegment(sketch, "E789", {"start": v(16.24, -27.72) * mm, "end": v(16.24, -27.72) * mm});
            skLineSegment(sketch, "E790", {"start": v(16.24, -27.72) * mm, "end": v(16.24, -27.73) * mm});
            skLineSegment(sketch, "E791", {"start": v(16.24, -27.73) * mm, "end": v(16.23, -27.73) * mm});
            skLineSegment(sketch, "E792", {"start": v(17.04, -27.24) * mm, "end": v(17, -27.26) * mm});
            skLineSegment(sketch, "E793", {"start": v(17, -27.26) * mm, "end": v(16.98, -27.28) * mm});
            skLineSegment(sketch, "E794", {"start": v(16.98, -27.28) * mm, "end": v(16.95, -27.3) * mm});
            skLineSegment(sketch, "E795", {"start": v(16.95, -27.3) * mm, "end": v(16.92, -27.3) * mm});
            skLineSegment(sketch, "E796", {"start": v(16.92, -27.3) * mm, "end": v(16.9, -27.33) * mm});
            skLineSegment(sketch, "E797", {"start": v(16.9, -27.33) * mm, "end": v(16.86, -27.34) * mm});
            skLineSegment(sketch, "E798", {"start": v(16.86, -27.34) * mm, "end": v(16.83, -27.36) * mm});
            skLineSegment(sketch, "E799", {"start": v(16.83, -27.36) * mm, "end": v(16.8, -27.38) * mm});
            skLineSegment(sketch, "E800", {"start": v(16.8, -27.38) * mm, "end": v(16.78, -27.4) * mm});
            skLineSegment(sketch, "E801", {"start": v(16.78, -27.4) * mm, "end": v(16.75, -27.41) * mm});
            skLineSegment(sketch, "E802", {"start": v(16.75, -27.41) * mm, "end": v(16.72, -27.43) * mm});
            skLineSegment(sketch, "E803", {"start": v(16.72, -27.43) * mm, "end": v(16.69, -27.44) * mm});
            skLineSegment(sketch, "E804", {"start": v(16.69, -27.44) * mm, "end": v(16.66, -27.46) * mm});
            skLineSegment(sketch, "E805", {"start": v(16.66, -27.46) * mm, "end": v(16.63, -27.48) * mm});
            skLineSegment(sketch, "E806", {"start": v(16.63, -27.48) * mm, "end": v(16.6, -27.5) * mm});
            skLineSegment(sketch, "E807", {"start": v(16.6, -27.5) * mm, "end": v(16.57, -27.51) * mm});
            skLineSegment(sketch, "E808", {"start": v(16.57, -27.51) * mm, "end": v(16.54, -27.53) * mm});
            skLineSegment(sketch, "E809", {"start": v(16.54, -27.53) * mm, "end": v(16.51, -27.54) * mm});
            skLineSegment(sketch, "E810", {"start": v(16.51, -27.54) * mm, "end": v(16.48, -27.56) * mm});
            skLineSegment(sketch, "E811", {"start": v(16.48, -27.56) * mm, "end": v(16.46, -27.58) * mm});
            skLineSegment(sketch, "E812", {"start": v(16.46, -27.58) * mm, "end": v(16.43, -27.6) * mm});
            skLineSegment(sketch, "E813", {"start": v(16.43, -27.6) * mm, "end": v(16.4, -27.61) * mm});
            skLineSegment(sketch, "E814", {"start": v(16.4, -27.61) * mm, "end": v(16.37, -27.63) * mm});
            skLineSegment(sketch, "E815", {"start": v(16.37, -27.63) * mm, "end": v(16.34, -27.65) * mm});
            skLineSegment(sketch, "E816", {"start": v(17.24, -26.9) * mm, "end": v(17.24, -26.91) * mm});
            skLineSegment(sketch, "E817", {"start": v(17.24, -26.91) * mm, "end": v(17.24, -26.93) * mm});
            skLineSegment(sketch, "E818", {"start": v(17.24, -26.93) * mm, "end": v(17.24, -26.95) * mm});
            skLineSegment(sketch, "E819", {"start": v(17.24, -26.95) * mm, "end": v(17.24, -26.96) * mm});
            skLineSegment(sketch, "E820", {"start": v(17.24, -26.96) * mm, "end": v(17.23, -26.98) * mm});
            skLineSegment(sketch, "E821", {"start": v(17.23, -26.98) * mm, "end": v(17.23, -27) * mm});
            skLineSegment(sketch, "E822", {"start": v(17.23, -27) * mm, "end": v(17.22, -27.01) * mm});
            skLineSegment(sketch, "E823", {"start": v(17.22, -27.01) * mm, "end": v(17.22, -27.03) * mm});
            skLineSegment(sketch, "E824", {"start": v(17.22, -27.03) * mm, "end": v(17.21, -27.05) * mm});
            skLineSegment(sketch, "E825", {"start": v(17.21, -27.05) * mm, "end": v(17.2, -27.06) * mm});
            skLineSegment(sketch, "E826", {"start": v(17.2, -27.06) * mm, "end": v(17.2, -27.08) * mm});
            skLineSegment(sketch, "E827", {"start": v(17.2, -27.08) * mm, "end": v(17.19, -27.1) * mm});
            skLineSegment(sketch, "E828", {"start": v(17.19, -27.1) * mm, "end": v(17.18, -27.1) * mm});
            skLineSegment(sketch, "E829", {"start": v(17.18, -27.1) * mm, "end": v(17.17, -27.12) * mm});
            skLineSegment(sketch, "E830", {"start": v(17.17, -27.12) * mm, "end": v(17.16, -27.14) * mm});
            skLineSegment(sketch, "E831", {"start": v(17.16, -27.14) * mm, "end": v(17.15, -27.15) * mm});
            skLineSegment(sketch, "E832", {"start": v(17.15, -27.15) * mm, "end": v(17.13, -27.17) * mm});
            skLineSegment(sketch, "E833", {"start": v(17.13, -27.17) * mm, "end": v(17.12, -27.18) * mm});
            skLineSegment(sketch, "E834", {"start": v(17.12, -27.18) * mm, "end": v(17.1, -27.2) * mm});
            skLineSegment(sketch, "E835", {"start": v(17.1, -27.2) * mm, "end": v(17.1, -27.2) * mm});
            skLineSegment(sketch, "E836", {"start": v(17.1, -27.2) * mm, "end": v(17.08, -27.21) * mm});
            skLineSegment(sketch, "E837", {"start": v(17.08, -27.21) * mm, "end": v(17.07, -27.22) * mm});
            skLineSegment(sketch, "E838", {"start": v(17.07, -27.22) * mm, "end": v(17.05, -27.23) * mm});
            skLineSegment(sketch, "E839", {"start": v(17.05, -27.23) * mm, "end": v(17.04, -27.24) * mm});
            skLineSegment(sketch, "E840", {"start": v(17.24, -26.88) * mm, "end": v(17.24, -26.9) * mm});
            skLineSegment(sketch, "E841", {"start": v(17.36, -26.88) * mm, "end": v(17.24, -26.88) * mm});
            skLineSegment(sketch, "E842", {"start": v(17.36, -22.56) * mm, "end": v(17.36, -26.88) * mm});
            skLineSegment(sketch, "E843", {"start": v(23.15, 20.45) * mm, "end": v(38.42, 20.45) * mm});
            skLineSegment(sketch, "E844", {"start": v(23.15, 14.8) * mm, "end": v(41.42, 14.8) * mm});
            skLineSegment(sketch, "E845", {"start": v(41.42, 14.8) * mm, "end": v(43.48, 14.8) * mm});
            skLineSegment(sketch, "E846", {"start": v(41.37, 20.45) * mm, "end": v(41.42, 14.8) * mm});
            skLineSegment(sketch, "E847", {"start": v(38.42, 20.45) * mm, "end": v(41.37, 20.45) * mm});
            skLineSegment(sketch, "E848", {"start": v(38.4, 22.5) * mm, "end": v(38.42, 20.45) * mm});
            skLineSegment(sketch, "E849", {"start": v(43.55, 22.5) * mm, "end": v(38.4, 22.5) * mm});
            skLineSegment(sketch, "E850", {"start": v(43.48, 14.8) * mm, "end": v(43.55, 22.5) * mm});
            skLineSegment(sketch, "E851", {"start": v(19.57, -23.8) * mm, "end": v(19.49, -37.94) * mm});
            skLineSegment(sketch, "E852", {"start": v(23.15, -23.8) * mm, "end": v(19.57, -23.8) * mm});
            skLineSegment(sketch, "E853", {"start": v(19.55, -23.8) * mm, "end": v(35.5, -23.8) * mm});
            skLineSegment(sketch, "E854", {"start": v(19.55, -36.65) * mm, "end": v(19.55, -23.8) * mm});
            skLineSegment(sketch, "E855", {"start": v(34.64, -21.74) * mm, "end": v(17.83, -21.74) * mm});
            skLineSegment(sketch, "E856", {"start": v(42.03, -14.35) * mm, "end": v(34.64, -21.74) * mm});
            skLineSegment(sketch, "E857", {"start": v(42.29, 14.8) * mm, "end": v(42.03, -14.35) * mm});
            skLineSegment(sketch, "E858", {"start": v(43.73, 14.8) * mm, "end": v(42.29, 14.8) * mm});
            skLineSegment(sketch, "E859", {"start": v(43.73, 37.94) * mm, "end": v(43.73, 14.8) * mm});
            skLineSegment(sketch, "E860", {"start": v(45.79, -13.5) * mm, "end": v(45.79, 37.94) * mm});
            skLineSegment(sketch, "E861", {"start": v(35.5, -23.8) * mm, "end": v(45.79, -13.5) * mm});
            skLineSegment(sketch, "E862", {"start": v(-45.79, 37.94) * mm, "end": v(-41.16, 37.94) * mm});
            skLineSegment(sketch, "E863", {"start": v(-23.15, 22.5) * mm, "end": v(-23.15, 14.8) * mm});
            skLineSegment(sketch, "E864", {"start": v(23.15, 22.5) * mm, "end": v(23.15, 14.8) * mm});
            skLineSegment(sketch, "E865", {"start": v(0, 40.32) * mm, "end": v(0, -42.42) * mm});
            skSolve(sketch);
        }
        {
            var Q0;
            Q0=makeQuery(id+"F0.imprint","IMPRINT",FACE,{"disambiguationData":[TD([[makeQuery(id+"F0.imprint","IMPRINT",EDGE,{"derivedFrom":sQuery(id+"F0.wireOp",EDGE,"E17")}),1.0]])]});
            var Q1;
            {var subQ0=sQuery(id+"F0.wireOp",EDGE,"E6");Q1=makeQuery(id+"F0.imprint","IMPRINT",FACE,{"disambiguationData":[TD([[makeQuery(id+"F0.imprint","IMPRINT",EDGE,{"derivedFrom":subQ0}),-1.0]])]});}
            var Q2;
            {var subQ0=sQuery(id+"F0.wireOp",EDGE,"E21");Q2=makeQuery(id+"F0.imprint","IMPRINT",FACE,{"disambiguationData":[TD([[makeQuery(id+"F0.imprint","IMPRINT",EDGE,{"derivedFrom":subQ0}),1.0]])]});}
            var Q3;
            {var subQ1=sQuery(id+"F0.wireOp",EDGE,"E15");Q3=makeQuery(id+"F0.imprint","IMPRINT",FACE,{"disambiguationData":[TD([[makeQuery(id+"F0.imprint","IMPRINT",EDGE,{"derivedFrom":subQ1}),1.0]])]});}
            var Q4;
            {var subQ1=sQuery(id+"F0.wireOp",EDGE,"E15");Q4=makeQuery(id+"F0.imprint","IMPRINT",FACE,{"disambiguationData":[TD([[makeQuery(id+"F0.imprint","IMPRINT",EDGE,{"derivedFrom":subQ1}),-1.0]])]});}
            var Q5;
            {var subQ3=sQuery(id+"F0.wireOp",EDGE,"b195d664-6227-49c4-8dac-1feb21df325d");Q5=makeQuery(id+"F0.imprint","IMPRINT",FACE,{"disambiguationData":[TD([[makeQuery(id+"F0.imprint","IMPRINT",EDGE,{"derivedFrom":subQ3}),1.0]])]});}
            var Q6;
            {var subQ1=sQuery(id+"F0.wireOp",EDGE,"08513299-fe9a-4478-9602-3b79bfce2925");Q6=makeQuery(id+"F0.imprint","IMPRINT",FACE,{"disambiguationData":[TD([[makeQuery(id+"F0.imprint","IMPRINT",EDGE,{"derivedFrom":subQ1}),-1.0]])]});}
            var Q7;
            Q7=sQuery(id+"F0.wireOp",EDGE,"E865");
            revolve(context, id + "F1", {"entities" : qUnion([Q0, Q1, Q2, Q3, Q4, Q5, Q6]), "axis" : qUnion([Q7]), "revolveType" : RevolveType.FULL});
        }
        {
            var Q0;
            Q0=makeQuery(id+"F1.opRevolve","SWEPT_FACE",FACE,{"disambiguationData":[OSD([sQuery(id+"F0.wireOp",EDGE,"E19"),sQuery(id+"F0.wireOp",EDGE,"E20")])]});
            var sketch = newSketch(context, id + "F2", { "sketchPlane" : qUnion([Q0])});
            skCircle(sketch, "E866", {"center": v(0, 33.5) * mm, "radius": 6 * mm});
            skCircle(sketch, "E867.1.0", {"center": v(-23.69, 23.69) * mm, "radius": 6 * mm});
            skCircle(sketch, "E867.2.0", {"center": v(-33.5, 0) * mm, "radius": 6 * mm});
            skCircle(sketch, "E867.3.0", {"center": v(-23.69, -23.69) * mm, "radius": 6 * mm});
            skCircle(sketch, "E867.4.0", {"center": v(0, -33.5) * mm, "radius": 6 * mm});
            skCircle(sketch, "E867.5.0", {"center": v(23.69, -23.69) * mm, "radius": 6 * mm});
            skCircle(sketch, "E867.6.0", {"center": v(33.5, 0) * mm, "radius": 6 * mm});
            skCircle(sketch, "E867.7.0", {"center": v(23.69, 23.69) * mm, "radius": 6 * mm});
            skPoint(sketch, "E867.center", {"position": v(0, 0) * mm});
            skSolve(sketch);
        }
        {
            var Q0;
            Q0=makeQuery(id+"F2.imprint","IMPRINT",FACE,{"disambiguationData":[TD([[makeQuery(id+"F2.imprint","IMPRINT",EDGE,{"derivedFrom":sQuery(id+"F2.wireOp",EDGE,"E866")}),1.0]])]});
            var Q1;
            Q1=makeQuery(id+"F2.imprint","IMPRINT",FACE,{"disambiguationData":[TD([[makeQuery(id+"F2.imprint","IMPRINT",EDGE,{"derivedFrom":sQuery(id+"F2.wireOp",EDGE,"E867.7.0")}),1.0]])]});
            var Q2;
            Q2=makeQuery(id+"F2.imprint","IMPRINT",FACE,{"disambiguationData":[TD([[makeQuery(id+"F2.imprint","IMPRINT",EDGE,{"derivedFrom":sQuery(id+"F2.wireOp",EDGE,"E867.6.0")}),1.0]])]});
            var Q3;
            Q3=makeQuery(id+"F2.imprint","IMPRINT",FACE,{"disambiguationData":[TD([[makeQuery(id+"F2.imprint","IMPRINT",EDGE,{"derivedFrom":sQuery(id+"F2.wireOp",EDGE,"E867.5.0")}),1.0]])]});
            var Q4;
            Q4=makeQuery(id+"F2.imprint","IMPRINT",FACE,{"disambiguationData":[TD([[makeQuery(id+"F2.imprint","IMPRINT",EDGE,{"derivedFrom":sQuery(id+"F2.wireOp",EDGE,"E867.4.0")}),1.0]])]});
            var Q5;
            Q5=makeQuery(id+"F2.imprint","IMPRINT",FACE,{"disambiguationData":[TD([[makeQuery(id+"F2.imprint","IMPRINT",EDGE,{"derivedFrom":sQuery(id+"F2.wireOp",EDGE,"E867.3.0")}),1.0]])]});
            var Q6;
            Q6=makeQuery(id+"F2.imprint","IMPRINT",FACE,{"disambiguationData":[TD([[makeQuery(id+"F2.imprint","IMPRINT",EDGE,{"derivedFrom":sQuery(id+"F2.wireOp",EDGE,"E867.2.0")}),1.0]])]});
            var Q7;
            Q7=makeQuery(id+"F2.imprint","IMPRINT",FACE,{"disambiguationData":[TD([[makeQuery(id+"F2.imprint","IMPRINT",EDGE,{"derivedFrom":sQuery(id+"F2.wireOp",EDGE,"E867.1.0")}),1.0]])]});
            extrude(context, id + "F3", {"entities" : qUnion([Q0, Q1, Q2, Q3, Q4, Q5, Q6, Q7]), "operationType" : NewBodyOperationType.REMOVE, "oppositeDirection" : true, "depth" : 12.5 * mm, "offsetDistance" : 25 * mm});
        }
    });
